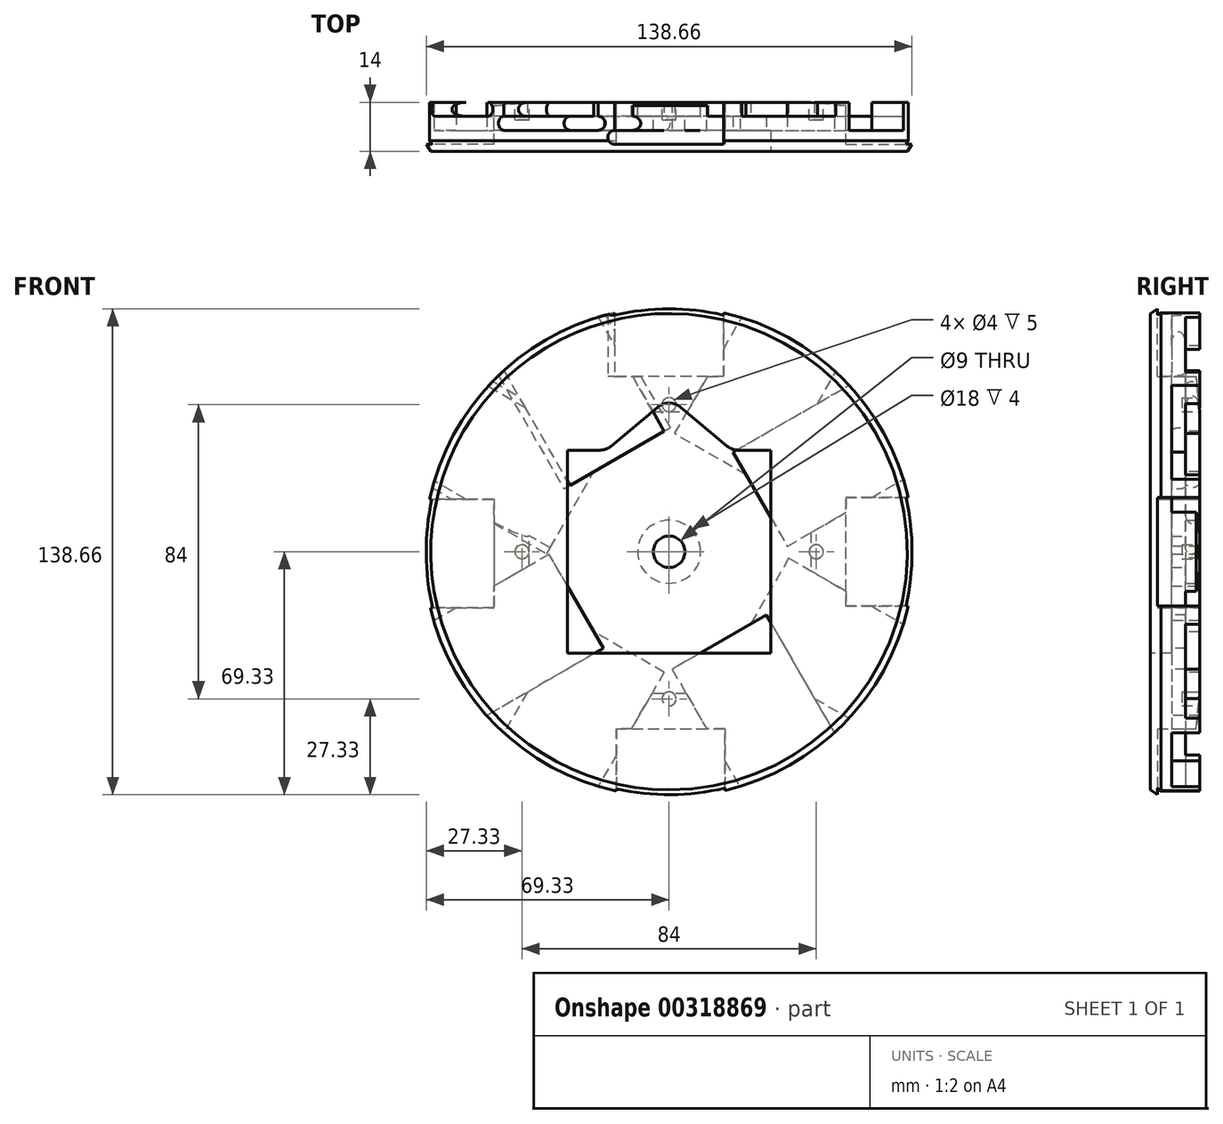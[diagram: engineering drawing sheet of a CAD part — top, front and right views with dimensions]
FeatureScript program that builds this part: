
annotation { "Feature Type Name" : "Feature", "Feature Type Description" : "" }
export const myFeature = defineFeature(function(context is Context, id is Id, definition is map)
    precondition{}
    {
        {
            var Q0;
            Q0=qCreatedBy(makeId("Front.planeOp"),FACE);
            var sketch = newSketch(context, id + "F0", { "sketchPlane" : qUnion([Q0])});
            skCircle(sketch, "E0", {"center": v(0, 0) * mm, "radius": 70 * mm});
            skCircle(sketch, "E1", {"center": v(0, 0) * mm, "radius": 50 * mm});
            skLineSegment(sketch, "E2", {"start": v(0, 50) * mm, "end": v(15.5, 50) * mm});
            skLineSegment(sketch, "E3.MirrorCS", {"start": v(0, 50) * mm, "end": v(-15.5, 50) * mm});
            skLineSegment(sketch, "E4", {"start": v(-15.5, 50) * mm, "end": v(-15.5, 87.34) * mm});
            skLineSegment(sketch, "E5.MirrorCS", {"start": v(15.5, 50) * mm, "end": v(15.5, 87.34) * mm});
            skCircle(sketch, "E6", {"center": v(0, 0) * mm, "radius": 30 * mm, "construction": true});
            skLineSegment(sketch, "E7", {"start": v(0, 0) * mm, "end": v(15, 25.98) * mm, "construction": true});
            skLineSegment(sketch, "E8", {"start": v(15, 25.98) * mm, "end": v(0, 0) * mm, "construction": true});
            skPoint(sketch, "E9.endSnap0", {"position": v(7.5, 13) * mm});
            skLineSegment(sketch, "E10", {"start": v(15, 25.98) * mm, "end": v(1.58, 33.73) * mm});
            skLineSegment(sketch, "E11.MirrorCS", {"start": v(15, 25.98) * mm, "end": v(28.42, 18.23) * mm});
            skLineSegment(sketch, "E12", {"start": v(1.58, 33.73) * mm, "end": v(33.76, 89.47) * mm});
            skLineSegment(sketch, "E13.MirrorCS", {"start": v(28.42, 18.23) * mm, "end": v(60.6, 73.97) * mm});
            skPoint(sketch, "E14.center", {"position": v(0, 10) * mm});
            skLineSegment(sketch, "E15", {"start": v(0, 0) * mm, "end": v(25.98, 15) * mm, "construction": true});
            skLineSegment(sketch, "E16", {"start": v(25.98, 15) * mm, "end": v(18.23, 28.42) * mm});
            skPoint(sketch, "E16.endSnap0", {"position": v(21.71, 22.1) * mm});
            skLineSegment(sketch, "E17", {"start": v(18.23, 28.42) * mm, "end": v(69.8, 58.2) * mm});
            skLineSegment(sketch, "E18.MirrorCS", {"start": v(25.98, 15) * mm, "end": v(33.73, 1.58) * mm});
            skLineSegment(sketch, "E19.MirrorCS", {"start": v(33.73, 1.58) * mm, "end": v(85.3, 31.35) * mm});
            skLineSegment(sketch, "E20.1.0", {"start": v(-50, -16) * mm, "end": v(-87.34, -16) * mm});
            skLineSegment(sketch, "E20.1.1", {"start": v(-50, -0.5) * mm, "end": v(-50, -16) * mm});
            skLineSegment(sketch, "E20.1.2", {"start": v(-50, -0.5) * mm, "end": v(-50, 15) * mm});
            skLineSegment(sketch, "E20.1.3", {"start": v(-50, 15) * mm, "end": v(-87.34, 15) * mm});
            skLineSegment(sketch, "E20.2.0", {"start": v(16, -50.5) * mm, "end": v(16, -87.84) * mm});
            skLineSegment(sketch, "E20.2.1", {"start": v(0.5, -50.5) * mm, "end": v(16, -50.5) * mm});
            skLineSegment(sketch, "E20.2.2", {"start": v(0.5, -50.5) * mm, "end": v(-15, -50.5) * mm});
            skLineSegment(sketch, "E20.2.3", {"start": v(-15, -50.5) * mm, "end": v(-15, -87.84) * mm});
            skLineSegment(sketch, "E20.3.0", {"start": v(50.5, 15.5) * mm, "end": v(87.84, 15.5) * mm});
            skLineSegment(sketch, "E20.3.1", {"start": v(50.5, 0) * mm, "end": v(50.5, 15.5) * mm});
            skLineSegment(sketch, "E20.3.2", {"start": v(50.5, 0) * mm, "end": v(50.5, -15.5) * mm});
            skLineSegment(sketch, "E20.3.3", {"start": v(50.5, -15.5) * mm, "end": v(87.84, -15.5) * mm});
            skPoint(sketch, "E20.center", {"position": v(0.25, -0.25) * mm});
            skLineSegment(sketch, "E21.1.0", {"start": v(-33.98, 1.14) * mm, "end": v(-89.72, 33.33) * mm});
            skLineSegment(sketch, "E21.1.1", {"start": v(-26.23, 14.57) * mm, "end": v(-33.98, 1.14) * mm});
            skLineSegment(sketch, "E21.1.2", {"start": v(-26.23, 14.57) * mm, "end": v(-18.48, 28) * mm});
            skLineSegment(sketch, "E21.1.3", {"start": v(-18.48, 28) * mm, "end": v(-74.22, 60.17) * mm});
            skLineSegment(sketch, "E21.2.0", {"start": v(-1.4, -34.41) * mm, "end": v(-33.58, -90.16) * mm});
            skLineSegment(sketch, "E21.2.1", {"start": v(-14.82, -26.66) * mm, "end": v(-1.4, -34.41) * mm});
            skLineSegment(sketch, "E21.2.2", {"start": v(-14.82, -26.66) * mm, "end": v(-28.24, -18.91) * mm});
            skLineSegment(sketch, "E21.2.3", {"start": v(-28.24, -18.91) * mm, "end": v(-60.42, -74.66) * mm});
            skLineSegment(sketch, "E21.3.0", {"start": v(34.16, -1.83) * mm, "end": v(89.9, -34) * mm});
            skLineSegment(sketch, "E21.3.1", {"start": v(26.41, -15.25) * mm, "end": v(34.16, -1.83) * mm});
            skLineSegment(sketch, "E21.3.2", {"start": v(26.41, -15.25) * mm, "end": v(18.66, -28.67) * mm});
            skLineSegment(sketch, "E21.3.3", {"start": v(18.66, -28.67) * mm, "end": v(74.4, -60.86) * mm});
            skPoint(sketch, "E21.center", {"position": v(0.1, -0.34) * mm});
            skLineSegment(sketch, "E22.1.0", {"start": v(-28.24, 18.91) * mm, "end": v(-58.01, 70.48) * mm});
            skLineSegment(sketch, "E22.1.1", {"start": v(-14.82, 26.66) * mm, "end": v(-28.24, 18.91) * mm});
            skLineSegment(sketch, "E22.1.2", {"start": v(-14.82, 26.66) * mm, "end": v(-1.4, 34.41) * mm});
            skLineSegment(sketch, "E22.1.3", {"start": v(-1.4, 34.41) * mm, "end": v(-31.17, 85.98) * mm});
            skLineSegment(sketch, "E22.2.0", {"start": v(-18.73, -27.56) * mm, "end": v(-70.3, -57.33) * mm});
            skLineSegment(sketch, "E22.2.1", {"start": v(-26.48, -14.13) * mm, "end": v(-18.73, -27.56) * mm});
            skLineSegment(sketch, "E22.2.2", {"start": v(-26.48, -14.13) * mm, "end": v(-34.23, -0.71) * mm});
            skLineSegment(sketch, "E22.2.3", {"start": v(-34.23, -0.71) * mm, "end": v(-85.8, -30.48) * mm});
            skLineSegment(sketch, "E22.3.0", {"start": v(27.74, -18.05) * mm, "end": v(57.51, -69.62) * mm});
            skLineSegment(sketch, "E22.3.1", {"start": v(14.32, -25.8) * mm, "end": v(27.74, -18.05) * mm});
            skLineSegment(sketch, "E22.3.2", {"start": v(14.32, -25.8) * mm, "end": v(0.9, -33.55) * mm});
            skLineSegment(sketch, "E22.3.3", {"start": v(0.9, -33.55) * mm, "end": v(30.67, -85.12) * mm});
            skPoint(sketch, "E22.center", {"position": v(-0.25, 0.43) * mm});
            skCircle(sketch, "E23", {"center": v(0, 0) * mm, "radius": 4.5 * mm});
            skSolve(sketch);
        }
        {
            var Q0;
            {var subQ9=sQuery(id+"F0.wireOp",EDGE,"E10");Q0=makeQuery(id+"F0.imprint","IMPRINT",FACE,{"disambiguationData":[TD([[makeQuery(id+"F0.imprint","IMPRINT",EDGE,{"derivedFrom":subQ9}),1.0]])]});}
            var Q1;
            {var subQ0=sQuery(id+"F0.wireOp",EDGE,"E21.1.1");Q1=makeQuery(id+"F0.imprint","IMPRINT",FACE,{"disambiguationData":[TD([[makeQuery(id+"F0.imprint","IMPRINT",EDGE,{"derivedFrom":subQ0}),-1.0]])]});}
            var Q2;
            {var subQ6=sQuery(id+"F0.wireOp",EDGE,"E0");var subQ12=sQuery(id+"F0.wireOp",EDGE,"E21.1.3");var subQ13=makeQuery(id+"F0.imprint","INTERSECT",VERTEX,{"derivedFrom":[subQ6,subQ12]});Q2=makeQuery(id+"F0.imprint","IMPRINT",FACE,{"disambiguationData":[TD([[makeQuery(id+"F0.imprint","IMPRINT",EDGE,{"disambiguationData":[TD([[subQ13,-1.0]])],"derivedFrom":subQ6}),1.0]])]});}
            var Q3;
            {var subQ0=sQuery(id+"F0.wireOp",EDGE,"E21.1.0");var subQ1=sQuery(id+"F0.wireOp",EDGE,"E0");var subQ2=makeQuery(id+"F0.imprint","INTERSECT",VERTEX,{"derivedFrom":[subQ1,subQ0]});Q3=makeQuery(id+"F0.imprint","IMPRINT",FACE,{"disambiguationData":[TD([[makeQuery(id+"F0.imprint","IMPRINT",EDGE,{"disambiguationData":[TD([[subQ2,-1.0]])],"derivedFrom":subQ1}),1.0]])]});}
            var Q4;
            {var subQ1=sQuery(id+"F0.wireOp",EDGE,"E1");var subQ3=sQuery(id+"F0.wireOp",EDGE,"E21.1.0");var subQ4=makeQuery(id+"F0.imprint","INTERSECT",VERTEX,{"derivedFrom":[subQ1,subQ3]});Q4=makeQuery(id+"F0.imprint","IMPRINT",FACE,{"disambiguationData":[TD([[makeQuery(id+"F0.imprint","IMPRINT",EDGE,{"disambiguationData":[TD([[subQ4,-1.0]])],"derivedFrom":subQ3}),1.0]])]});}
            var Q5;
            {var subQ1=sQuery(id+"F0.wireOp",EDGE,"E1");var subQ3=sQuery(id+"F0.wireOp",EDGE,"E22.2.3");var subQ4=makeQuery(id+"F0.imprint","INTERSECT",VERTEX,{"derivedFrom":[subQ1,subQ3]});Q5=makeQuery(id+"F0.imprint","IMPRINT",FACE,{"disambiguationData":[TD([[makeQuery(id+"F0.imprint","IMPRINT",EDGE,{"disambiguationData":[TD([[subQ4,-1.0]])],"derivedFrom":subQ3}),-1.0]])]});}
            var Q6;
            {var subQ3=sQuery(id+"F0.wireOp",EDGE,"E22.2.3");var subQ6=sQuery(id+"F0.wireOp",EDGE,"E0");var subQ14=makeQuery(id+"F0.imprint","INTERSECT",VERTEX,{"derivedFrom":[subQ6,subQ3]});Q6=makeQuery(id+"F0.imprint","IMPRINT",FACE,{"disambiguationData":[TD([[makeQuery(id+"F0.imprint","IMPRINT",EDGE,{"disambiguationData":[TD([[subQ14,-1.0]])],"derivedFrom":subQ6}),1.0]])]});}
            var Q7;
            {var subQ0=sQuery(id+"F0.wireOp",EDGE,"E22.2.2");Q7=makeQuery(id+"F0.imprint","IMPRINT",FACE,{"disambiguationData":[TD([[makeQuery(id+"F0.imprint","IMPRINT",EDGE,{"derivedFrom":subQ0}),1.0]])]});}
            var Q8;
            {var subQ0=sQuery(id+"F0.wireOp",EDGE,"E20.1.0");var subQ1=sQuery(id+"F0.wireOp",EDGE,"E0");var subQ2=makeQuery(id+"F0.imprint","INTERSECT",VERTEX,{"derivedFrom":[subQ1,subQ0]});Q8=makeQuery(id+"F0.imprint","IMPRINT",FACE,{"disambiguationData":[TD([[makeQuery(id+"F0.imprint","IMPRINT",EDGE,{"disambiguationData":[TD([[subQ2,-1.0]])],"derivedFrom":subQ1}),1.0]])]});}
            var Q9;
            {var subQ0=sQuery(id+"F0.wireOp",EDGE,"E22.2.0");var subQ1=sQuery(id+"F0.wireOp",EDGE,"E0");var subQ2=makeQuery(id+"F0.imprint","INTERSECT",VERTEX,{"derivedFrom":[subQ1,subQ0]});Q9=makeQuery(id+"F0.imprint","IMPRINT",FACE,{"disambiguationData":[TD([[makeQuery(id+"F0.imprint","IMPRINT",EDGE,{"disambiguationData":[TD([[subQ2,-1.0]])],"derivedFrom":subQ1}),1.0]])]});}
            var Q10;
            {var subQ0=sQuery(id+"F0.wireOp",EDGE,"E21.2.0");var subQ1=sQuery(id+"F0.wireOp",EDGE,"E0");var subQ2=makeQuery(id+"F0.imprint","INTERSECT",VERTEX,{"derivedFrom":[subQ1,subQ0]});Q10=makeQuery(id+"F0.imprint","IMPRINT",FACE,{"disambiguationData":[TD([[makeQuery(id+"F0.imprint","IMPRINT",EDGE,{"disambiguationData":[TD([[subQ2,-1.0]])],"derivedFrom":subQ1}),1.0]])]});}
            var Q11;
            {var subQ0=sQuery(id+"F0.wireOp",EDGE,"E21.2.3");var subQ3=sQuery(id+"F0.wireOp",EDGE,"E1");var subQ4=makeQuery(id+"F0.imprint","INTERSECT",VERTEX,{"derivedFrom":[subQ3,subQ0]});Q11=makeQuery(id+"F0.imprint","IMPRINT",FACE,{"disambiguationData":[TD([[makeQuery(id+"F0.imprint","IMPRINT",EDGE,{"disambiguationData":[TD([[subQ4,-1.0]])],"derivedFrom":subQ3}),1.0]])]});}
            var Q12;
            {var subQ0=sQuery(id+"F0.wireOp",EDGE,"E21.2.1");Q12=makeQuery(id+"F0.imprint","IMPRINT",FACE,{"disambiguationData":[TD([[makeQuery(id+"F0.imprint","IMPRINT",EDGE,{"derivedFrom":subQ0}),-1.0]])]});}
            var Q13;
            {var subQ0=sQuery(id+"F0.wireOp",EDGE,"E21.2.3");var subQ1=sQuery(id+"F0.wireOp",EDGE,"E1");var subQ2=makeQuery(id+"F0.imprint","INTERSECT",VERTEX,{"derivedFrom":[subQ1,subQ0]});Q13=makeQuery(id+"F0.imprint","IMPRINT",FACE,{"disambiguationData":[TD([[makeQuery(id+"F0.imprint","IMPRINT",EDGE,{"disambiguationData":[TD([[subQ2,-1.0]])],"derivedFrom":subQ1}),-1.0]])]});}
            var Q14;
            {var subQ9=sQuery(id+"F0.wireOp",EDGE,"E21.2.3");var subQ10=sQuery(id+"F0.wireOp",EDGE,"E0");var subQ11=makeQuery(id+"F0.imprint","INTERSECT",VERTEX,{"derivedFrom":[subQ10,subQ9]});Q14=makeQuery(id+"F0.imprint","IMPRINT",FACE,{"disambiguationData":[TD([[makeQuery(id+"F0.imprint","IMPRINT",EDGE,{"disambiguationData":[TD([[subQ11,-1.0]])],"derivedFrom":subQ10}),1.0]])]});}
            var Q15;
            {var subQ1=sQuery(id+"F0.wireOp",EDGE,"E1");var subQ3=sQuery(id+"F0.wireOp",EDGE,"E21.2.0");var subQ4=makeQuery(id+"F0.imprint","INTERSECT",VERTEX,{"derivedFrom":[subQ1,subQ3]});Q15=makeQuery(id+"F0.imprint","IMPRINT",FACE,{"disambiguationData":[TD([[makeQuery(id+"F0.imprint","IMPRINT",EDGE,{"disambiguationData":[TD([[subQ4,-1.0]])],"derivedFrom":subQ3}),1.0]])]});}
            var Q16;
            {var subQ1=sQuery(id+"F0.wireOp",EDGE,"E1");var subQ3=sQuery(id+"F0.wireOp",EDGE,"E22.3.3");var subQ4=makeQuery(id+"F0.imprint","INTERSECT",VERTEX,{"derivedFrom":[subQ1,subQ3]});Q16=makeQuery(id+"F0.imprint","IMPRINT",FACE,{"disambiguationData":[TD([[makeQuery(id+"F0.imprint","IMPRINT",EDGE,{"disambiguationData":[TD([[subQ4,-1.0]])],"derivedFrom":subQ3}),-1.0]])]});}
            var Q17;
            {var subQ0=sQuery(id+"F0.wireOp",EDGE,"E20.2.0");var subQ1=sQuery(id+"F0.wireOp",EDGE,"E0");var subQ2=makeQuery(id+"F0.imprint","INTERSECT",VERTEX,{"derivedFrom":[subQ1,subQ0]});Q17=makeQuery(id+"F0.imprint","IMPRINT",FACE,{"disambiguationData":[TD([[makeQuery(id+"F0.imprint","IMPRINT",EDGE,{"disambiguationData":[TD([[subQ2,-1.0]])],"derivedFrom":subQ1}),1.0]])]});}
            var Q18;
            {var subQ0=sQuery(id+"F0.wireOp",EDGE,"E22.3.2");Q18=makeQuery(id+"F0.imprint","IMPRINT",FACE,{"disambiguationData":[TD([[makeQuery(id+"F0.imprint","IMPRINT",EDGE,{"derivedFrom":subQ0}),1.0]])]});}
            var Q19;
            {var subQ3=sQuery(id+"F0.wireOp",EDGE,"E22.3.3");var subQ12=sQuery(id+"F0.wireOp",EDGE,"E0");var subQ13=makeQuery(id+"F0.imprint","INTERSECT",VERTEX,{"derivedFrom":[subQ12,subQ3]});Q19=makeQuery(id+"F0.imprint","IMPRINT",FACE,{"disambiguationData":[TD([[makeQuery(id+"F0.imprint","IMPRINT",EDGE,{"disambiguationData":[TD([[subQ13,-1.0]])],"derivedFrom":subQ12}),1.0]])]});}
            var Q20;
            {var subQ0=sQuery(id+"F0.wireOp",EDGE,"E21.3.3");var subQ3=sQuery(id+"F0.wireOp",EDGE,"E1");var subQ4=makeQuery(id+"F0.imprint","INTERSECT",VERTEX,{"derivedFrom":[subQ3,subQ0]});Q20=makeQuery(id+"F0.imprint","IMPRINT",FACE,{"disambiguationData":[TD([[makeQuery(id+"F0.imprint","IMPRINT",EDGE,{"disambiguationData":[TD([[subQ4,-1.0]])],"derivedFrom":subQ3}),1.0]])]});}
            var Q21;
            {var subQ0=sQuery(id+"F0.wireOp",EDGE,"E21.3.1");Q21=makeQuery(id+"F0.imprint","IMPRINT",FACE,{"disambiguationData":[TD([[makeQuery(id+"F0.imprint","IMPRINT",EDGE,{"derivedFrom":subQ0}),-1.0]])]});}
            var Q22;
            {var subQ0=sQuery(id+"F0.wireOp",EDGE,"E21.3.3");var subQ1=sQuery(id+"F0.wireOp",EDGE,"E1");var subQ2=makeQuery(id+"F0.imprint","INTERSECT",VERTEX,{"derivedFrom":[subQ1,subQ0]});Q22=makeQuery(id+"F0.imprint","IMPRINT",FACE,{"disambiguationData":[TD([[makeQuery(id+"F0.imprint","IMPRINT",EDGE,{"disambiguationData":[TD([[subQ2,-1.0]])],"derivedFrom":subQ1}),-1.0]])]});}
            var Q23;
            {var subQ0=sQuery(id+"F0.wireOp",EDGE,"E22.3.0");var subQ1=sQuery(id+"F0.wireOp",EDGE,"E0");var subQ2=makeQuery(id+"F0.imprint","INTERSECT",VERTEX,{"derivedFrom":[subQ1,subQ0]});Q23=makeQuery(id+"F0.imprint","IMPRINT",FACE,{"disambiguationData":[TD([[makeQuery(id+"F0.imprint","IMPRINT",EDGE,{"disambiguationData":[TD([[subQ2,-1.0]])],"derivedFrom":subQ1}),1.0]])]});}
            var Q24;
            {var subQ10=sQuery(id+"F0.wireOp",EDGE,"E0");var subQ12=sQuery(id+"F0.wireOp",EDGE,"E21.3.3");var subQ13=makeQuery(id+"F0.imprint","INTERSECT",VERTEX,{"derivedFrom":[subQ10,subQ12]});Q24=makeQuery(id+"F0.imprint","IMPRINT",FACE,{"disambiguationData":[TD([[makeQuery(id+"F0.imprint","IMPRINT",EDGE,{"disambiguationData":[TD([[subQ13,-1.0]])],"derivedFrom":subQ10}),1.0]])]});}
            var Q25;
            {var subQ1=sQuery(id+"F0.wireOp",EDGE,"E1");var subQ3=sQuery(id+"F0.wireOp",EDGE,"E21.3.0");var subQ4=makeQuery(id+"F0.imprint","INTERSECT",VERTEX,{"derivedFrom":[subQ1,subQ3]});Q25=makeQuery(id+"F0.imprint","IMPRINT",FACE,{"disambiguationData":[TD([[makeQuery(id+"F0.imprint","IMPRINT",EDGE,{"disambiguationData":[TD([[subQ4,-1.0]])],"derivedFrom":subQ3}),1.0]])]});}
            var Q26;
            {var subQ1=sQuery(id+"F0.wireOp",EDGE,"E1");var subQ3=sQuery(id+"F0.wireOp",EDGE,"E19.MirrorCS");var subQ4=makeQuery(id+"F0.imprint","INTERSECT",VERTEX,{"derivedFrom":[subQ1,subQ3]});Q26=makeQuery(id+"F0.imprint","IMPRINT",FACE,{"disambiguationData":[TD([[makeQuery(id+"F0.imprint","IMPRINT",EDGE,{"disambiguationData":[TD([[subQ4,-1.0]])],"derivedFrom":subQ3}),-1.0]])]});}
            var Q27;
            {var subQ0=sQuery(id+"F0.wireOp",EDGE,"E18.MirrorCS");Q27=makeQuery(id+"F0.imprint","IMPRINT",FACE,{"disambiguationData":[TD([[makeQuery(id+"F0.imprint","IMPRINT",EDGE,{"derivedFrom":subQ0}),1.0]])]});}
            var Q28;
            {var subQ5=sQuery(id+"F0.wireOp",EDGE,"E19.MirrorCS");var subQ6=sQuery(id+"F0.wireOp",EDGE,"E0");var subQ7=makeQuery(id+"F0.imprint","INTERSECT",VERTEX,{"derivedFrom":[subQ6,subQ5]});Q28=makeQuery(id+"F0.imprint","IMPRINT",FACE,{"disambiguationData":[TD([[makeQuery(id+"F0.imprint","IMPRINT",EDGE,{"disambiguationData":[TD([[subQ7,-1.0]])],"derivedFrom":subQ6}),1.0]])]});}
            var Q29;
            {var subQ0=sQuery(id+"F0.wireOp",EDGE,"E19.MirrorCS");var subQ1=sQuery(id+"F0.wireOp",EDGE,"E0");var subQ2=makeQuery(id+"F0.imprint","INTERSECT",VERTEX,{"derivedFrom":[subQ1,subQ0]});Q29=makeQuery(id+"F0.imprint","IMPRINT",FACE,{"disambiguationData":[TD([[makeQuery(id+"F0.imprint","IMPRINT",EDGE,{"disambiguationData":[TD([[subQ2,1.0]])],"derivedFrom":subQ1}),1.0]])]});}
            var Q30;
            {var subQ5=sQuery(id+"F0.wireOp",EDGE,"E13.MirrorCS");var subQ7=sQuery(id+"F0.wireOp",EDGE,"E1");var subQ8=makeQuery(id+"F0.imprint","INTERSECT",VERTEX,{"derivedFrom":[subQ7,subQ5]});Q30=makeQuery(id+"F0.imprint","IMPRINT",FACE,{"disambiguationData":[TD([[makeQuery(id+"F0.imprint","IMPRINT",EDGE,{"disambiguationData":[TD([[subQ8,-1.0]])],"derivedFrom":subQ7}),1.0]])]});}
            var Q31;
            {var subQ1=sQuery(id+"F0.wireOp",EDGE,"E10");Q31=makeQuery(id+"F0.imprint","IMPRINT",FACE,{"disambiguationData":[TD([[makeQuery(id+"F0.imprint","IMPRINT",EDGE,{"derivedFrom":subQ1}),-1.0]])]});}
            var Q32;
            {var subQ0=sQuery(id+"F0.wireOp",EDGE,"E13.MirrorCS");var subQ1=sQuery(id+"F0.wireOp",EDGE,"E1");var subQ2=makeQuery(id+"F0.imprint","INTERSECT",VERTEX,{"derivedFrom":[subQ1,subQ0]});Q32=makeQuery(id+"F0.imprint","IMPRINT",FACE,{"disambiguationData":[TD([[makeQuery(id+"F0.imprint","IMPRINT",EDGE,{"disambiguationData":[TD([[subQ2,-1.0]])],"derivedFrom":subQ1}),-1.0]])]});}
            var Q33;
            {var subQ5=sQuery(id+"F0.wireOp",EDGE,"E13.MirrorCS");var subQ6=sQuery(id+"F0.wireOp",EDGE,"E0");var subQ7=makeQuery(id+"F0.imprint","INTERSECT",VERTEX,{"derivedFrom":[subQ6,subQ5]});Q33=makeQuery(id+"F0.imprint","IMPRINT",FACE,{"disambiguationData":[TD([[makeQuery(id+"F0.imprint","IMPRINT",EDGE,{"disambiguationData":[TD([[subQ7,-1.0]])],"derivedFrom":subQ6}),1.0]])]});}
            var Q34;
            {var subQ0=sQuery(id+"F0.wireOp",EDGE,"E17");var subQ1=sQuery(id+"F0.wireOp",EDGE,"E0");var subQ2=makeQuery(id+"F0.imprint","INTERSECT",VERTEX,{"derivedFrom":[subQ1,subQ0]});Q34=makeQuery(id+"F0.imprint","IMPRINT",FACE,{"disambiguationData":[TD([[makeQuery(id+"F0.imprint","IMPRINT",EDGE,{"disambiguationData":[TD([[subQ2,-1.0]])],"derivedFrom":subQ1}),1.0]])]});}
            var Q35;
            {var subQ0=sQuery(id+"F0.wireOp",EDGE,"E12");var subQ1=sQuery(id+"F0.wireOp",EDGE,"E0");var subQ2=makeQuery(id+"F0.imprint","INTERSECT",VERTEX,{"derivedFrom":[subQ1,subQ0]});Q35=makeQuery(id+"F0.imprint","IMPRINT",FACE,{"disambiguationData":[TD([[makeQuery(id+"F0.imprint","IMPRINT",EDGE,{"disambiguationData":[TD([[subQ2,-1.0]])],"derivedFrom":subQ1}),1.0]])]});}
            var Q36;
            {var subQ1=sQuery(id+"F0.wireOp",EDGE,"E1");var subQ3=sQuery(id+"F0.wireOp",EDGE,"E12");var subQ4=makeQuery(id+"F0.imprint","INTERSECT",VERTEX,{"derivedFrom":[subQ1,subQ3]});Q36=makeQuery(id+"F0.imprint","IMPRINT",FACE,{"disambiguationData":[TD([[makeQuery(id+"F0.imprint","IMPRINT",EDGE,{"disambiguationData":[TD([[subQ4,-1.0]])],"derivedFrom":subQ3}),1.0]])]});}
            var Q37;
            {var subQ1=sQuery(id+"F0.wireOp",EDGE,"E1");var subQ3=sQuery(id+"F0.wireOp",EDGE,"E22.1.3");var subQ4=makeQuery(id+"F0.imprint","INTERSECT",VERTEX,{"derivedFrom":[subQ1,subQ3]});Q37=makeQuery(id+"F0.imprint","IMPRINT",FACE,{"disambiguationData":[TD([[makeQuery(id+"F0.imprint","IMPRINT",EDGE,{"disambiguationData":[TD([[subQ4,-1.0]])],"derivedFrom":subQ3}),-1.0]])]});}
            var Q38;
            {var subQ0=sQuery(id+"F0.wireOp",EDGE,"E22.1.2");Q38=makeQuery(id+"F0.imprint","IMPRINT",FACE,{"disambiguationData":[TD([[makeQuery(id+"F0.imprint","IMPRINT",EDGE,{"derivedFrom":subQ0}),1.0]])]});}
            var Q39;
            {var subQ0=sQuery(id+"F0.wireOp",EDGE,"E21.1.3");var subQ3=sQuery(id+"F0.wireOp",EDGE,"E1");var subQ4=makeQuery(id+"F0.imprint","INTERSECT",VERTEX,{"derivedFrom":[subQ3,subQ0]});Q39=makeQuery(id+"F0.imprint","IMPRINT",FACE,{"disambiguationData":[TD([[makeQuery(id+"F0.imprint","IMPRINT",EDGE,{"disambiguationData":[TD([[subQ4,-1.0]])],"derivedFrom":subQ3}),1.0]])]});}
            var Q40;
            {var subQ0=sQuery(id+"F0.wireOp",EDGE,"E21.1.3");var subQ1=sQuery(id+"F0.wireOp",EDGE,"E1");var subQ2=makeQuery(id+"F0.imprint","INTERSECT",VERTEX,{"derivedFrom":[subQ1,subQ0]});Q40=makeQuery(id+"F0.imprint","IMPRINT",FACE,{"disambiguationData":[TD([[makeQuery(id+"F0.imprint","IMPRINT",EDGE,{"disambiguationData":[TD([[subQ2,-1.0]])],"derivedFrom":subQ1}),-1.0]])]});}
            var Q41;
            {var subQ0=sQuery(id+"F0.wireOp",EDGE,"E22.1.0");var subQ1=sQuery(id+"F0.wireOp",EDGE,"E0");var subQ2=makeQuery(id+"F0.imprint","INTERSECT",VERTEX,{"derivedFrom":[subQ1,subQ0]});Q41=makeQuery(id+"F0.imprint","IMPRINT",FACE,{"disambiguationData":[TD([[makeQuery(id+"F0.imprint","IMPRINT",EDGE,{"disambiguationData":[TD([[subQ2,-1.0]])],"derivedFrom":subQ1}),1.0]])]});}
            var Q42;
            {var subQ3=sQuery(id+"F0.wireOp",EDGE,"E22.1.3");var subQ10=sQuery(id+"F0.wireOp",EDGE,"E0");var subQ11=makeQuery(id+"F0.imprint","INTERSECT",VERTEX,{"derivedFrom":[subQ10,subQ3]});Q42=makeQuery(id+"F0.imprint","IMPRINT",FACE,{"disambiguationData":[TD([[makeQuery(id+"F0.imprint","IMPRINT",EDGE,{"disambiguationData":[TD([[subQ11,-1.0]])],"derivedFrom":subQ10}),1.0]])]});}
            var Q43;
            {var subQ0=sQuery(id+"F0.wireOp",EDGE,"E4");var subQ1=sQuery(id+"F0.wireOp",EDGE,"E0");var subQ2=makeQuery(id+"F0.imprint","INTERSECT",VERTEX,{"derivedFrom":[subQ1,subQ0]});Q43=makeQuery(id+"F0.imprint","IMPRINT",FACE,{"disambiguationData":[TD([[makeQuery(id+"F0.imprint","IMPRINT",EDGE,{"disambiguationData":[TD([[subQ2,-1.0]])],"derivedFrom":subQ1}),1.0]])]});}
            var Q44;
            {var subQ0=sQuery(id+"F0.wireOp",EDGE,"E21.3.0");var subQ1=sQuery(id+"F0.wireOp",EDGE,"E0");var subQ2=makeQuery(id+"F0.imprint","INTERSECT",VERTEX,{"derivedFrom":[subQ1,subQ0]});Q44=makeQuery(id+"F0.imprint","IMPRINT",FACE,{"disambiguationData":[TD([[makeQuery(id+"F0.imprint","IMPRINT",EDGE,{"disambiguationData":[TD([[subQ2,-1.0]])],"derivedFrom":subQ1}),1.0]])]});}
            var Q45;
            {var subQ0=sQuery(id+"F0.wireOp",EDGE,"E4");var subQ1=sQuery(id+"F0.wireOp",EDGE,"E3.MirrorCS");var subQ2=makeQuery(id+"F0.imprint","INTERSECT",VERTEX,{"derivedFrom":[subQ1,subQ0]});Q45=makeQuery(id+"F0.imprint","IMPRINT",FACE,{"disambiguationData":[TD([[makeQuery(id+"F0.imprint","IMPRINT",EDGE,{"disambiguationData":[TD([[subQ2,1.0]])],"derivedFrom":subQ1}),-1.0]])]});}
            var Q46;
            {var subQ7=sQuery(id+"F0.wireOp",EDGE,"E5.MirrorCS");var subQ11=sQuery(id+"F0.wireOp",EDGE,"E0");var subQ13=makeQuery(id+"F0.imprint","INTERSECT",VERTEX,{"derivedFrom":[subQ11,subQ7]});Q46=makeQuery(id+"F0.imprint","IMPRINT",FACE,{"disambiguationData":[TD([[makeQuery(id+"F0.imprint","IMPRINT",EDGE,{"disambiguationData":[TD([[subQ13,-1.0]])],"derivedFrom":subQ11}),1.0]])]});}
            var Q47;
            {var subQ0=sQuery(id+"F0.wireOp",EDGE,"E5.MirrorCS");var subQ1=sQuery(id+"F0.wireOp",EDGE,"E2");var subQ2=makeQuery(id+"F0.imprint","INTERSECT",VERTEX,{"derivedFrom":[subQ1,subQ0]});Q47=makeQuery(id+"F0.imprint","IMPRINT",FACE,{"disambiguationData":[TD([[makeQuery(id+"F0.imprint","IMPRINT",EDGE,{"disambiguationData":[TD([[subQ2,1.0]])],"derivedFrom":subQ1}),1.0]])]});}
            var Q48;
            {var subQ6=sQuery(id+"F0.wireOp",EDGE,"E0");var subQ11=sQuery(id+"F0.wireOp",EDGE,"E20.1.3");var subQ13=makeQuery(id+"F0.imprint","INTERSECT",VERTEX,{"derivedFrom":[subQ6,subQ11]});Q48=makeQuery(id+"F0.imprint","IMPRINT",FACE,{"disambiguationData":[TD([[makeQuery(id+"F0.imprint","IMPRINT",EDGE,{"disambiguationData":[TD([[subQ13,-1.0]])],"derivedFrom":subQ6}),1.0]])]});}
            var Q49;
            {var subQ0=sQuery(id+"F0.wireOp",EDGE,"E20.1.3");var subQ1=sQuery(id+"F0.wireOp",EDGE,"E20.1.2");var subQ2=makeQuery(id+"F0.imprint","INTERSECT",VERTEX,{"derivedFrom":[subQ1,subQ0]});Q49=makeQuery(id+"F0.imprint","IMPRINT",FACE,{"disambiguationData":[TD([[makeQuery(id+"F0.imprint","IMPRINT",EDGE,{"disambiguationData":[TD([[subQ2,1.0]])],"derivedFrom":subQ1}),1.0]])]});}
            var Q50;
            {var subQ0=sQuery(id+"F0.wireOp",EDGE,"E20.1.1");var subQ1=sQuery(id+"F0.wireOp",EDGE,"E20.1.0");var subQ2=makeQuery(id+"F0.imprint","INTERSECT",VERTEX,{"derivedFrom":[subQ1,subQ0]});Q50=makeQuery(id+"F0.imprint","IMPRINT",FACE,{"disambiguationData":[TD([[makeQuery(id+"F0.imprint","IMPRINT",EDGE,{"disambiguationData":[TD([[subQ2,-1.0]])],"derivedFrom":subQ1}),-1.0]])]});}
            var Q51;
            {var subQ6=sQuery(id+"F0.wireOp",EDGE,"E0");var subQ11=sQuery(id+"F0.wireOp",EDGE,"E20.2.3");var subQ12=makeQuery(id+"F0.imprint","INTERSECT",VERTEX,{"derivedFrom":[subQ6,subQ11]});Q51=makeQuery(id+"F0.imprint","IMPRINT",FACE,{"disambiguationData":[TD([[makeQuery(id+"F0.imprint","IMPRINT",EDGE,{"disambiguationData":[TD([[subQ12,-1.0]])],"derivedFrom":subQ6}),1.0]])]});}
            var Q52;
            {var subQ0=sQuery(id+"F0.wireOp",EDGE,"E20.2.3");var subQ1=sQuery(id+"F0.wireOp",EDGE,"E20.2.2");var subQ2=makeQuery(id+"F0.imprint","INTERSECT",VERTEX,{"derivedFrom":[subQ1,subQ0]});Q52=makeQuery(id+"F0.imprint","IMPRINT",FACE,{"disambiguationData":[TD([[makeQuery(id+"F0.imprint","IMPRINT",EDGE,{"disambiguationData":[TD([[subQ2,1.0]])],"derivedFrom":subQ1}),1.0]])]});}
            var Q53;
            {var subQ0=sQuery(id+"F0.wireOp",EDGE,"E20.2.1");var subQ1=sQuery(id+"F0.wireOp",EDGE,"E20.2.0");var subQ2=makeQuery(id+"F0.imprint","INTERSECT",VERTEX,{"derivedFrom":[subQ1,subQ0]});Q53=makeQuery(id+"F0.imprint","IMPRINT",FACE,{"disambiguationData":[TD([[makeQuery(id+"F0.imprint","IMPRINT",EDGE,{"disambiguationData":[TD([[subQ2,-1.0]])],"derivedFrom":subQ1}),-1.0]])]});}
            var Q54;
            {var subQ0=sQuery(id+"F0.wireOp",EDGE,"E20.3.3");var subQ1=sQuery(id+"F0.wireOp",EDGE,"E20.3.2");var subQ2=makeQuery(id+"F0.imprint","INTERSECT",VERTEX,{"derivedFrom":[subQ1,subQ0]});Q54=makeQuery(id+"F0.imprint","IMPRINT",FACE,{"disambiguationData":[TD([[makeQuery(id+"F0.imprint","IMPRINT",EDGE,{"disambiguationData":[TD([[subQ2,1.0]])],"derivedFrom":subQ1}),1.0]])]});}
            var Q55;
            {var subQ0=sQuery(id+"F0.wireOp",EDGE,"E20.3.0");var subQ1=sQuery(id+"F0.wireOp",EDGE,"E0");var subQ2=makeQuery(id+"F0.imprint","INTERSECT",VERTEX,{"derivedFrom":[subQ1,subQ0]});Q55=makeQuery(id+"F0.imprint","IMPRINT",FACE,{"disambiguationData":[TD([[makeQuery(id+"F0.imprint","IMPRINT",EDGE,{"disambiguationData":[TD([[subQ2,1.0]])],"derivedFrom":subQ1}),1.0]])]});}
            var Q56;
            {var subQ0=sQuery(id+"F0.wireOp",EDGE,"E20.3.1");var subQ1=sQuery(id+"F0.wireOp",EDGE,"E19.MirrorCS");var subQ2=makeQuery(id+"F0.imprint","INTERSECT",VERTEX,{"derivedFrom":[subQ1,subQ0]});Q56=makeQuery(id+"F0.imprint","IMPRINT",FACE,{"disambiguationData":[TD([[makeQuery(id+"F0.imprint","IMPRINT",EDGE,{"disambiguationData":[TD([[subQ2,-1.0]])],"derivedFrom":subQ1}),1.0]])]});}
            extrude(context, id + "F1", {"entities" : qUnion([Q0, Q1, Q2, Q3, Q4, Q5, Q6, Q7, Q8, Q9, Q10, Q11, Q12, Q13, Q14, Q15, Q16, Q17, Q18, Q19, Q20, Q21, Q22, Q23, Q24, Q25, Q26, Q27, Q28, Q29, Q30, Q31, Q32, Q33, Q34, Q35, Q36, Q37, Q38, Q39, Q40, Q41, Q42, Q43, Q44, Q45, Q46, Q47, Q48, Q49, Q50, Q51, Q52, Q53, Q54, Q55, Q56]), "offsetDistance" : 25 * mm, "depth" : 6 * mm});
        }
        {
            var Q0;
            {var subQ0=sQuery(id+"F0.wireOp",EDGE,"E19.MirrorCS");var subQ1=sQuery(id+"F0.wireOp",EDGE,"E0");var subQ2=makeQuery(id+"F0.imprint","INTERSECT",VERTEX,{"derivedFrom":[subQ1,subQ0]});Q0=makeQuery(id+"F0.imprint","IMPRINT",FACE,{"disambiguationData":[TD([[makeQuery(id+"F0.imprint","IMPRINT",EDGE,{"disambiguationData":[TD([[subQ2,1.0]])],"derivedFrom":subQ1}),1.0]])]});}
            var Q1;
            {var subQ0=sQuery(id+"F0.wireOp",EDGE,"E20.3.0");var subQ1=sQuery(id+"F0.wireOp",EDGE,"E0");var subQ2=makeQuery(id+"F0.imprint","INTERSECT",VERTEX,{"derivedFrom":[subQ1,subQ0]});Q1=makeQuery(id+"F0.imprint","IMPRINT",FACE,{"disambiguationData":[TD([[makeQuery(id+"F0.imprint","IMPRINT",EDGE,{"disambiguationData":[TD([[subQ2,1.0]])],"derivedFrom":subQ1}),1.0]])]});}
            var Q2;
            {var subQ9=sQuery(id+"F0.wireOp",EDGE,"E10");Q2=makeQuery(id+"F0.imprint","IMPRINT",FACE,{"disambiguationData":[TD([[makeQuery(id+"F0.imprint","IMPRINT",EDGE,{"derivedFrom":subQ9}),1.0]])]});}
            var Q3;
            {var subQ1=sQuery(id+"F0.wireOp",EDGE,"E1");var subQ3=sQuery(id+"F0.wireOp",EDGE,"E19.MirrorCS");var subQ4=makeQuery(id+"F0.imprint","INTERSECT",VERTEX,{"derivedFrom":[subQ1,subQ3]});Q3=makeQuery(id+"F0.imprint","IMPRINT",FACE,{"disambiguationData":[TD([[makeQuery(id+"F0.imprint","IMPRINT",EDGE,{"disambiguationData":[TD([[subQ4,-1.0]])],"derivedFrom":subQ3}),-1.0]])]});}
            var Q4;
            {var subQ1=sQuery(id+"F0.wireOp",EDGE,"E1");var subQ3=sQuery(id+"F0.wireOp",EDGE,"E21.3.0");var subQ4=makeQuery(id+"F0.imprint","INTERSECT",VERTEX,{"derivedFrom":[subQ1,subQ3]});Q4=makeQuery(id+"F0.imprint","IMPRINT",FACE,{"disambiguationData":[TD([[makeQuery(id+"F0.imprint","IMPRINT",EDGE,{"disambiguationData":[TD([[subQ4,-1.0]])],"derivedFrom":subQ3}),1.0]])]});}
            var Q5;
            {var subQ1=sQuery(id+"F0.wireOp",EDGE,"E1");var subQ3=sQuery(id+"F0.wireOp",EDGE,"E12");var subQ4=makeQuery(id+"F0.imprint","INTERSECT",VERTEX,{"derivedFrom":[subQ1,subQ3]});Q5=makeQuery(id+"F0.imprint","IMPRINT",FACE,{"disambiguationData":[TD([[makeQuery(id+"F0.imprint","IMPRINT",EDGE,{"disambiguationData":[TD([[subQ4,-1.0]])],"derivedFrom":subQ3}),1.0]])]});}
            var Q6;
            {var subQ1=sQuery(id+"F0.wireOp",EDGE,"E1");var subQ3=sQuery(id+"F0.wireOp",EDGE,"E22.1.3");var subQ4=makeQuery(id+"F0.imprint","INTERSECT",VERTEX,{"derivedFrom":[subQ1,subQ3]});Q6=makeQuery(id+"F0.imprint","IMPRINT",FACE,{"disambiguationData":[TD([[makeQuery(id+"F0.imprint","IMPRINT",EDGE,{"disambiguationData":[TD([[subQ4,-1.0]])],"derivedFrom":subQ3}),-1.0]])]});}
            var Q7;
            {var subQ7=sQuery(id+"F0.wireOp",EDGE,"E5.MirrorCS");var subQ11=sQuery(id+"F0.wireOp",EDGE,"E0");var subQ13=makeQuery(id+"F0.imprint","INTERSECT",VERTEX,{"derivedFrom":[subQ11,subQ7]});Q7=makeQuery(id+"F0.imprint","IMPRINT",FACE,{"disambiguationData":[TD([[makeQuery(id+"F0.imprint","IMPRINT",EDGE,{"disambiguationData":[TD([[subQ13,-1.0]])],"derivedFrom":subQ11}),1.0]])]});}
            var Q8;
            {var subQ0=sQuery(id+"F0.wireOp",EDGE,"E12");var subQ1=sQuery(id+"F0.wireOp",EDGE,"E0");var subQ2=makeQuery(id+"F0.imprint","INTERSECT",VERTEX,{"derivedFrom":[subQ1,subQ0]});Q8=makeQuery(id+"F0.imprint","IMPRINT",FACE,{"disambiguationData":[TD([[makeQuery(id+"F0.imprint","IMPRINT",EDGE,{"disambiguationData":[TD([[subQ2,-1.0]])],"derivedFrom":subQ1}),1.0]])]});}
            var Q9;
            {var subQ0=sQuery(id+"F0.wireOp",EDGE,"E17");var subQ1=sQuery(id+"F0.wireOp",EDGE,"E0");var subQ2=makeQuery(id+"F0.imprint","INTERSECT",VERTEX,{"derivedFrom":[subQ1,subQ0]});Q9=makeQuery(id+"F0.imprint","IMPRINT",FACE,{"disambiguationData":[TD([[makeQuery(id+"F0.imprint","IMPRINT",EDGE,{"disambiguationData":[TD([[subQ2,-1.0]])],"derivedFrom":subQ1}),1.0]])]});}
            var Q10;
            {var subQ0=sQuery(id+"F0.wireOp",EDGE,"E4");var subQ1=sQuery(id+"F0.wireOp",EDGE,"E0");var subQ2=makeQuery(id+"F0.imprint","INTERSECT",VERTEX,{"derivedFrom":[subQ1,subQ0]});Q10=makeQuery(id+"F0.imprint","IMPRINT",FACE,{"disambiguationData":[TD([[makeQuery(id+"F0.imprint","IMPRINT",EDGE,{"disambiguationData":[TD([[subQ2,-1.0]])],"derivedFrom":subQ1}),1.0]])]});}
            var Q11;
            {var subQ0=sQuery(id+"F0.wireOp",EDGE,"E22.1.0");var subQ1=sQuery(id+"F0.wireOp",EDGE,"E0");var subQ2=makeQuery(id+"F0.imprint","INTERSECT",VERTEX,{"derivedFrom":[subQ1,subQ0]});Q11=makeQuery(id+"F0.imprint","IMPRINT",FACE,{"disambiguationData":[TD([[makeQuery(id+"F0.imprint","IMPRINT",EDGE,{"disambiguationData":[TD([[subQ2,-1.0]])],"derivedFrom":subQ1}),1.0]])]});}
            var Q12;
            {var subQ0=sQuery(id+"F0.wireOp",EDGE,"E21.1.0");var subQ1=sQuery(id+"F0.wireOp",EDGE,"E0");var subQ2=makeQuery(id+"F0.imprint","INTERSECT",VERTEX,{"derivedFrom":[subQ1,subQ0]});Q12=makeQuery(id+"F0.imprint","IMPRINT",FACE,{"disambiguationData":[TD([[makeQuery(id+"F0.imprint","IMPRINT",EDGE,{"disambiguationData":[TD([[subQ2,-1.0]])],"derivedFrom":subQ1}),1.0]])]});}
            var Q13;
            {var subQ1=sQuery(id+"F0.wireOp",EDGE,"E1");var subQ3=sQuery(id+"F0.wireOp",EDGE,"E21.1.0");var subQ4=makeQuery(id+"F0.imprint","INTERSECT",VERTEX,{"derivedFrom":[subQ1,subQ3]});Q13=makeQuery(id+"F0.imprint","IMPRINT",FACE,{"disambiguationData":[TD([[makeQuery(id+"F0.imprint","IMPRINT",EDGE,{"disambiguationData":[TD([[subQ4,-1.0]])],"derivedFrom":subQ3}),1.0]])]});}
            var Q14;
            {var subQ1=sQuery(id+"F0.wireOp",EDGE,"E1");var subQ3=sQuery(id+"F0.wireOp",EDGE,"E22.2.3");var subQ4=makeQuery(id+"F0.imprint","INTERSECT",VERTEX,{"derivedFrom":[subQ1,subQ3]});Q14=makeQuery(id+"F0.imprint","IMPRINT",FACE,{"disambiguationData":[TD([[makeQuery(id+"F0.imprint","IMPRINT",EDGE,{"disambiguationData":[TD([[subQ4,-1.0]])],"derivedFrom":subQ3}),-1.0]])]});}
            var Q15;
            {var subQ6=sQuery(id+"F0.wireOp",EDGE,"E0");var subQ11=sQuery(id+"F0.wireOp",EDGE,"E20.1.3");var subQ13=makeQuery(id+"F0.imprint","INTERSECT",VERTEX,{"derivedFrom":[subQ6,subQ11]});Q15=makeQuery(id+"F0.imprint","IMPRINT",FACE,{"disambiguationData":[TD([[makeQuery(id+"F0.imprint","IMPRINT",EDGE,{"disambiguationData":[TD([[subQ13,-1.0]])],"derivedFrom":subQ6}),1.0]])]});}
            var Q16;
            {var subQ0=sQuery(id+"F0.wireOp",EDGE,"E20.1.0");var subQ1=sQuery(id+"F0.wireOp",EDGE,"E0");var subQ2=makeQuery(id+"F0.imprint","INTERSECT",VERTEX,{"derivedFrom":[subQ1,subQ0]});Q16=makeQuery(id+"F0.imprint","IMPRINT",FACE,{"disambiguationData":[TD([[makeQuery(id+"F0.imprint","IMPRINT",EDGE,{"disambiguationData":[TD([[subQ2,-1.0]])],"derivedFrom":subQ1}),1.0]])]});}
            var Q17;
            {var subQ0=sQuery(id+"F0.wireOp",EDGE,"E21.3.0");var subQ1=sQuery(id+"F0.wireOp",EDGE,"E0");var subQ2=makeQuery(id+"F0.imprint","INTERSECT",VERTEX,{"derivedFrom":[subQ1,subQ0]});Q17=makeQuery(id+"F0.imprint","IMPRINT",FACE,{"disambiguationData":[TD([[makeQuery(id+"F0.imprint","IMPRINT",EDGE,{"disambiguationData":[TD([[subQ2,-1.0]])],"derivedFrom":subQ1}),1.0]])]});}
            var Q18;
            {var subQ0=sQuery(id+"F0.wireOp",EDGE,"E22.3.0");var subQ1=sQuery(id+"F0.wireOp",EDGE,"E0");var subQ2=makeQuery(id+"F0.imprint","INTERSECT",VERTEX,{"derivedFrom":[subQ1,subQ0]});Q18=makeQuery(id+"F0.imprint","IMPRINT",FACE,{"disambiguationData":[TD([[makeQuery(id+"F0.imprint","IMPRINT",EDGE,{"disambiguationData":[TD([[subQ2,-1.0]])],"derivedFrom":subQ1}),1.0]])]});}
            var Q19;
            {var subQ0=sQuery(id+"F0.wireOp",EDGE,"E20.2.0");var subQ1=sQuery(id+"F0.wireOp",EDGE,"E0");var subQ2=makeQuery(id+"F0.imprint","INTERSECT",VERTEX,{"derivedFrom":[subQ1,subQ0]});Q19=makeQuery(id+"F0.imprint","IMPRINT",FACE,{"disambiguationData":[TD([[makeQuery(id+"F0.imprint","IMPRINT",EDGE,{"disambiguationData":[TD([[subQ2,-1.0]])],"derivedFrom":subQ1}),1.0]])]});}
            var Q20;
            {var subQ6=sQuery(id+"F0.wireOp",EDGE,"E0");var subQ11=sQuery(id+"F0.wireOp",EDGE,"E20.2.3");var subQ12=makeQuery(id+"F0.imprint","INTERSECT",VERTEX,{"derivedFrom":[subQ6,subQ11]});Q20=makeQuery(id+"F0.imprint","IMPRINT",FACE,{"disambiguationData":[TD([[makeQuery(id+"F0.imprint","IMPRINT",EDGE,{"disambiguationData":[TD([[subQ12,-1.0]])],"derivedFrom":subQ6}),1.0]])]});}
            var Q21;
            {var subQ1=sQuery(id+"F0.wireOp",EDGE,"E1");var subQ3=sQuery(id+"F0.wireOp",EDGE,"E22.3.3");var subQ4=makeQuery(id+"F0.imprint","INTERSECT",VERTEX,{"derivedFrom":[subQ1,subQ3]});Q21=makeQuery(id+"F0.imprint","IMPRINT",FACE,{"disambiguationData":[TD([[makeQuery(id+"F0.imprint","IMPRINT",EDGE,{"disambiguationData":[TD([[subQ4,-1.0]])],"derivedFrom":subQ3}),-1.0]])]});}
            var Q22;
            {var subQ1=sQuery(id+"F0.wireOp",EDGE,"E1");var subQ3=sQuery(id+"F0.wireOp",EDGE,"E21.2.0");var subQ4=makeQuery(id+"F0.imprint","INTERSECT",VERTEX,{"derivedFrom":[subQ1,subQ3]});Q22=makeQuery(id+"F0.imprint","IMPRINT",FACE,{"disambiguationData":[TD([[makeQuery(id+"F0.imprint","IMPRINT",EDGE,{"disambiguationData":[TD([[subQ4,-1.0]])],"derivedFrom":subQ3}),1.0]])]});}
            var Q23;
            {var subQ0=sQuery(id+"F0.wireOp",EDGE,"E21.2.0");var subQ1=sQuery(id+"F0.wireOp",EDGE,"E0");var subQ2=makeQuery(id+"F0.imprint","INTERSECT",VERTEX,{"derivedFrom":[subQ1,subQ0]});Q23=makeQuery(id+"F0.imprint","IMPRINT",FACE,{"disambiguationData":[TD([[makeQuery(id+"F0.imprint","IMPRINT",EDGE,{"disambiguationData":[TD([[subQ2,-1.0]])],"derivedFrom":subQ1}),1.0]])]});}
            var Q24;
            {var subQ0=sQuery(id+"F0.wireOp",EDGE,"E22.2.0");var subQ1=sQuery(id+"F0.wireOp",EDGE,"E0");var subQ2=makeQuery(id+"F0.imprint","INTERSECT",VERTEX,{"derivedFrom":[subQ1,subQ0]});Q24=makeQuery(id+"F0.imprint","IMPRINT",FACE,{"disambiguationData":[TD([[makeQuery(id+"F0.imprint","IMPRINT",EDGE,{"disambiguationData":[TD([[subQ2,-1.0]])],"derivedFrom":subQ1}),1.0]])]});}
            extrude(context, id + "F2", {"entities" : qUnion([Q0, Q1, Q2, Q3, Q4, Q5, Q6, Q7, Q8, Q9, Q10, Q11, Q12, Q13, Q14, Q15, Q16, Q17, Q18, Q19, Q20, Q21, Q22, Q23, Q24]), "operationType" : NewBodyOperationType.ADD, "oppositeDirection" : true, "depth" : 8 * mm});
        }
        {
            var Q0;
            {var subQ5=sQuery(id+"F0.wireOp",EDGE,"E13.MirrorCS");var subQ6=sQuery(id+"F0.wireOp",EDGE,"E0");var subQ7=makeQuery(id+"F0.imprint","INTERSECT",VERTEX,{"derivedFrom":[subQ6,subQ5]});Q0=makeQuery(id+"F0.imprint","IMPRINT",FACE,{"disambiguationData":[TD([[makeQuery(id+"F0.imprint","IMPRINT",EDGE,{"disambiguationData":[TD([[subQ7,-1.0]])],"derivedFrom":subQ6}),1.0]])]});}
            var Q1;
            {var subQ0=sQuery(id+"F0.wireOp",EDGE,"E5.MirrorCS");var subQ1=sQuery(id+"F0.wireOp",EDGE,"E2");var subQ2=makeQuery(id+"F0.imprint","INTERSECT",VERTEX,{"derivedFrom":[subQ1,subQ0]});Q1=makeQuery(id+"F0.imprint","IMPRINT",FACE,{"disambiguationData":[TD([[makeQuery(id+"F0.imprint","IMPRINT",EDGE,{"disambiguationData":[TD([[subQ2,1.0]])],"derivedFrom":subQ1}),1.0]])]});}
            var Q2;
            {var subQ1=sQuery(id+"F0.wireOp",EDGE,"E10");Q2=makeQuery(id+"F0.imprint","IMPRINT",FACE,{"disambiguationData":[TD([[makeQuery(id+"F0.imprint","IMPRINT",EDGE,{"derivedFrom":subQ1}),-1.0]])]});}
            var Q3;
            {var subQ0=sQuery(id+"F0.wireOp",EDGE,"E20.1.3");var subQ1=sQuery(id+"F0.wireOp",EDGE,"E20.1.2");var subQ2=makeQuery(id+"F0.imprint","INTERSECT",VERTEX,{"derivedFrom":[subQ1,subQ0]});Q3=makeQuery(id+"F0.imprint","IMPRINT",FACE,{"disambiguationData":[TD([[makeQuery(id+"F0.imprint","IMPRINT",EDGE,{"disambiguationData":[TD([[subQ2,1.0]])],"derivedFrom":subQ1}),1.0]])]});}
            var Q4;
            {var subQ0=sQuery(id+"F0.wireOp",EDGE,"E21.1.1");Q4=makeQuery(id+"F0.imprint","IMPRINT",FACE,{"disambiguationData":[TD([[makeQuery(id+"F0.imprint","IMPRINT",EDGE,{"derivedFrom":subQ0}),-1.0]])]});}
            var Q5;
            {var subQ6=sQuery(id+"F0.wireOp",EDGE,"E0");var subQ12=sQuery(id+"F0.wireOp",EDGE,"E21.1.3");var subQ13=makeQuery(id+"F0.imprint","INTERSECT",VERTEX,{"derivedFrom":[subQ6,subQ12]});Q5=makeQuery(id+"F0.imprint","IMPRINT",FACE,{"disambiguationData":[TD([[makeQuery(id+"F0.imprint","IMPRINT",EDGE,{"disambiguationData":[TD([[subQ13,-1.0]])],"derivedFrom":subQ6}),1.0]])]});}
            var Q6;
            {var subQ0=sQuery(id+"F0.wireOp",EDGE,"E20.2.3");var subQ1=sQuery(id+"F0.wireOp",EDGE,"E20.2.2");var subQ2=makeQuery(id+"F0.imprint","INTERSECT",VERTEX,{"derivedFrom":[subQ1,subQ0]});Q6=makeQuery(id+"F0.imprint","IMPRINT",FACE,{"disambiguationData":[TD([[makeQuery(id+"F0.imprint","IMPRINT",EDGE,{"disambiguationData":[TD([[subQ2,1.0]])],"derivedFrom":subQ1}),1.0]])]});}
            var Q7;
            {var subQ0=sQuery(id+"F0.wireOp",EDGE,"E21.2.1");Q7=makeQuery(id+"F0.imprint","IMPRINT",FACE,{"disambiguationData":[TD([[makeQuery(id+"F0.imprint","IMPRINT",EDGE,{"derivedFrom":subQ0}),-1.0]])]});}
            var Q8;
            {var subQ9=sQuery(id+"F0.wireOp",EDGE,"E21.2.3");var subQ10=sQuery(id+"F0.wireOp",EDGE,"E0");var subQ11=makeQuery(id+"F0.imprint","INTERSECT",VERTEX,{"derivedFrom":[subQ10,subQ9]});Q8=makeQuery(id+"F0.imprint","IMPRINT",FACE,{"disambiguationData":[TD([[makeQuery(id+"F0.imprint","IMPRINT",EDGE,{"disambiguationData":[TD([[subQ11,-1.0]])],"derivedFrom":subQ10}),1.0]])]});}
            var Q9;
            {var subQ10=sQuery(id+"F0.wireOp",EDGE,"E0");var subQ12=sQuery(id+"F0.wireOp",EDGE,"E21.3.3");var subQ13=makeQuery(id+"F0.imprint","INTERSECT",VERTEX,{"derivedFrom":[subQ10,subQ12]});Q9=makeQuery(id+"F0.imprint","IMPRINT",FACE,{"disambiguationData":[TD([[makeQuery(id+"F0.imprint","IMPRINT",EDGE,{"disambiguationData":[TD([[subQ13,-1.0]])],"derivedFrom":subQ10}),1.0]])]});}
            var Q10;
            {var subQ0=sQuery(id+"F0.wireOp",EDGE,"E21.3.1");Q10=makeQuery(id+"F0.imprint","IMPRINT",FACE,{"disambiguationData":[TD([[makeQuery(id+"F0.imprint","IMPRINT",EDGE,{"derivedFrom":subQ0}),-1.0]])]});}
            var Q11;
            {var subQ0=sQuery(id+"F0.wireOp",EDGE,"E20.3.3");var subQ1=sQuery(id+"F0.wireOp",EDGE,"E20.3.2");var subQ2=makeQuery(id+"F0.imprint","INTERSECT",VERTEX,{"derivedFrom":[subQ1,subQ0]});Q11=makeQuery(id+"F0.imprint","IMPRINT",FACE,{"disambiguationData":[TD([[makeQuery(id+"F0.imprint","IMPRINT",EDGE,{"disambiguationData":[TD([[subQ2,1.0]])],"derivedFrom":subQ1}),1.0]])]});}
            extrude(context, id + "F3", {"entities" : qUnion([Q0, Q1, Q2, Q3, Q4, Q5, Q6, Q7, Q8, Q9, Q10, Q11]), "operationType" : NewBodyOperationType.ADD, "oppositeDirection" : true, "depth" : 4 * mm});
        }
        {
            var Q0;
            {var subQ7=sQuery(id+"F0.wireOp",EDGE,"E5.MirrorCS");var subQ11=sQuery(id+"F0.wireOp",EDGE,"E0");var subQ13=makeQuery(id+"F0.imprint","INTERSECT",VERTEX,{"derivedFrom":[subQ11,subQ7]});Q0=makeQuery(id+"F0.imprint","IMPRINT",FACE,{"disambiguationData":[TD([[makeQuery(id+"F0.imprint","IMPRINT",EDGE,{"disambiguationData":[TD([[subQ13,-1.0]])],"derivedFrom":subQ11}),1.0]])]});}
            var Q1;
            {var subQ0=sQuery(id+"F0.wireOp",EDGE,"E4");var subQ1=sQuery(id+"F0.wireOp",EDGE,"E3.MirrorCS");var subQ2=makeQuery(id+"F0.imprint","INTERSECT",VERTEX,{"derivedFrom":[subQ1,subQ0]});Q1=makeQuery(id+"F0.imprint","IMPRINT",FACE,{"disambiguationData":[TD([[makeQuery(id+"F0.imprint","IMPRINT",EDGE,{"disambiguationData":[TD([[subQ2,1.0]])],"derivedFrom":subQ1}),-1.0]])]});}
            var Q2;
            {var subQ0=sQuery(id+"F0.wireOp",EDGE,"E5.MirrorCS");var subQ1=sQuery(id+"F0.wireOp",EDGE,"E2");var subQ2=makeQuery(id+"F0.imprint","INTERSECT",VERTEX,{"derivedFrom":[subQ1,subQ0]});Q2=makeQuery(id+"F0.imprint","IMPRINT",FACE,{"disambiguationData":[TD([[makeQuery(id+"F0.imprint","IMPRINT",EDGE,{"disambiguationData":[TD([[subQ2,1.0]])],"derivedFrom":subQ1}),1.0]])]});}
            var Q3;
            {var subQ0=sQuery(id+"F0.wireOp",EDGE,"E20.3.1");var subQ1=sQuery(id+"F0.wireOp",EDGE,"E19.MirrorCS");var subQ2=makeQuery(id+"F0.imprint","INTERSECT",VERTEX,{"derivedFrom":[subQ1,subQ0]});Q3=makeQuery(id+"F0.imprint","IMPRINT",FACE,{"disambiguationData":[TD([[makeQuery(id+"F0.imprint","IMPRINT",EDGE,{"disambiguationData":[TD([[subQ2,-1.0]])],"derivedFrom":subQ1}),1.0]])]});}
            var Q4;
            {var subQ0=sQuery(id+"F0.wireOp",EDGE,"E20.3.0");var subQ1=sQuery(id+"F0.wireOp",EDGE,"E0");var subQ2=makeQuery(id+"F0.imprint","INTERSECT",VERTEX,{"derivedFrom":[subQ1,subQ0]});Q4=makeQuery(id+"F0.imprint","IMPRINT",FACE,{"disambiguationData":[TD([[makeQuery(id+"F0.imprint","IMPRINT",EDGE,{"disambiguationData":[TD([[subQ2,1.0]])],"derivedFrom":subQ1}),1.0]])]});}
            var Q5;
            {var subQ0=sQuery(id+"F0.wireOp",EDGE,"E20.3.3");var subQ1=sQuery(id+"F0.wireOp",EDGE,"E20.3.2");var subQ2=makeQuery(id+"F0.imprint","INTERSECT",VERTEX,{"derivedFrom":[subQ1,subQ0]});Q5=makeQuery(id+"F0.imprint","IMPRINT",FACE,{"disambiguationData":[TD([[makeQuery(id+"F0.imprint","IMPRINT",EDGE,{"disambiguationData":[TD([[subQ2,1.0]])],"derivedFrom":subQ1}),1.0]])]});}
            var Q6;
            {var subQ0=sQuery(id+"F0.wireOp",EDGE,"E20.2.1");var subQ1=sQuery(id+"F0.wireOp",EDGE,"E20.2.0");var subQ2=makeQuery(id+"F0.imprint","INTERSECT",VERTEX,{"derivedFrom":[subQ1,subQ0]});Q6=makeQuery(id+"F0.imprint","IMPRINT",FACE,{"disambiguationData":[TD([[makeQuery(id+"F0.imprint","IMPRINT",EDGE,{"disambiguationData":[TD([[subQ2,-1.0]])],"derivedFrom":subQ1}),-1.0]])]});}
            var Q7;
            {var subQ0=sQuery(id+"F0.wireOp",EDGE,"E20.2.3");var subQ1=sQuery(id+"F0.wireOp",EDGE,"E20.2.2");var subQ2=makeQuery(id+"F0.imprint","INTERSECT",VERTEX,{"derivedFrom":[subQ1,subQ0]});Q7=makeQuery(id+"F0.imprint","IMPRINT",FACE,{"disambiguationData":[TD([[makeQuery(id+"F0.imprint","IMPRINT",EDGE,{"disambiguationData":[TD([[subQ2,1.0]])],"derivedFrom":subQ1}),1.0]])]});}
            var Q8;
            {var subQ6=sQuery(id+"F0.wireOp",EDGE,"E0");var subQ11=sQuery(id+"F0.wireOp",EDGE,"E20.2.3");var subQ12=makeQuery(id+"F0.imprint","INTERSECT",VERTEX,{"derivedFrom":[subQ6,subQ11]});Q8=makeQuery(id+"F0.imprint","IMPRINT",FACE,{"disambiguationData":[TD([[makeQuery(id+"F0.imprint","IMPRINT",EDGE,{"disambiguationData":[TD([[subQ12,-1.0]])],"derivedFrom":subQ6}),1.0]])]});}
            var Q9;
            {var subQ0=sQuery(id+"F0.wireOp",EDGE,"E20.1.1");var subQ1=sQuery(id+"F0.wireOp",EDGE,"E20.1.0");var subQ2=makeQuery(id+"F0.imprint","INTERSECT",VERTEX,{"derivedFrom":[subQ1,subQ0]});Q9=makeQuery(id+"F0.imprint","IMPRINT",FACE,{"disambiguationData":[TD([[makeQuery(id+"F0.imprint","IMPRINT",EDGE,{"disambiguationData":[TD([[subQ2,-1.0]])],"derivedFrom":subQ1}),-1.0]])]});}
            var Q10;
            {var subQ6=sQuery(id+"F0.wireOp",EDGE,"E0");var subQ11=sQuery(id+"F0.wireOp",EDGE,"E20.1.3");var subQ13=makeQuery(id+"F0.imprint","INTERSECT",VERTEX,{"derivedFrom":[subQ6,subQ11]});Q10=makeQuery(id+"F0.imprint","IMPRINT",FACE,{"disambiguationData":[TD([[makeQuery(id+"F0.imprint","IMPRINT",EDGE,{"disambiguationData":[TD([[subQ13,-1.0]])],"derivedFrom":subQ6}),1.0]])]});}
            var Q11;
            {var subQ0=sQuery(id+"F0.wireOp",EDGE,"E20.1.3");var subQ1=sQuery(id+"F0.wireOp",EDGE,"E20.1.2");var subQ2=makeQuery(id+"F0.imprint","INTERSECT",VERTEX,{"derivedFrom":[subQ1,subQ0]});Q11=makeQuery(id+"F0.imprint","IMPRINT",FACE,{"disambiguationData":[TD([[makeQuery(id+"F0.imprint","IMPRINT",EDGE,{"disambiguationData":[TD([[subQ2,1.0]])],"derivedFrom":subQ1}),1.0]])]});}
            extrude(context, id + "F4", {"entities" : qUnion([Q0, Q1, Q2, Q3, Q4, Q5, Q6, Q7, Q8, Q9, Q10, Q11]), "operationType" : NewBodyOperationType.REMOVE, "depth" : 4 * mm, "hasSecondDirection" : true, "secondDirectionOppositeDirection" : true, "secondDirectionDepth" : 10 * mm});
        }
        {
            var Q0;
            Q0=makeQuery(id+"F1.opExtrude","CAP_FACE",FACE,{"disambiguationData":[OSD([sQuery(id+"F0.wireOp",EDGE,"E0"),sQuery(id+"F0.wireOp",EDGE,"E23")])],"isStart":false});
            var sketch = newSketch(context, id + "F5", { "sketchPlane" : qUnion([Q0])});
            skLineSegment(sketch, "E24.bottom", {"start": v(29, -29) * mm, "end": v(-29, -29) * mm});
            skLineSegment(sketch, "E24.top", {"start": v(29, 29) * mm, "end": v(-29, 29) * mm});
            skLineSegment(sketch, "E24.left", {"start": v(29, -29) * mm, "end": v(29, 29) * mm});
            skLineSegment(sketch, "E24.right", {"start": v(-29, -29) * mm, "end": v(-29, 29) * mm});
            skPoint(sketch, "E24.middle", {"position": v(0, 0) * mm});
            skLineSegment(sketch, "E25", {"start": v(-18, 29) * mm, "end": v(0, 44) * mm});
            skLineSegment(sketch, "E26.MirrorCS", {"start": v(18, 29) * mm, "end": v(0, 44) * mm});
            skSolve(sketch);
        }
        {
            var Q0;
            Q0=makeQuery(id+"F5.imprint","IMPRINT",FACE,{"disambiguationData":[TD([[makeQuery(id+"F5.imprint","IMPRINT",EDGE,{"derivedFrom":sQuery(id+"F5.wireOp",EDGE,"E24.bottom")}),-1.0]])]});
            var Q1;
            {var subQ0=sQuery(id+"F5.wireOp",EDGE,"E25");Q1=makeQuery(id+"F5.imprint","IMPRINT",FACE,{"disambiguationData":[TD([[makeQuery(id+"F5.imprint","IMPRINT",EDGE,{"derivedFrom":subQ0}),-1.0]])]});}
            extrude(context, id + "F6", {"entities" : qUnion([Q0, Q1]), "operationType" : NewBodyOperationType.REMOVE, "oppositeDirection" : true, "offsetDistance" : 25 * mm, "depth" : 6 * mm});
        }
        {
            var Q0;
            Q0=makeQuery(id+"F6.boolean.opBoolean","COPY",EDGE,{"derivedFrom":makeQuery(id+"F6.opExtrude","SWEPT_EDGE",EDGE,{"disambiguationData":[OSD([sQuery(id+"F5.wireOp",EDGE,"E25"),sQuery(id+"F5.wireOp",EDGE,"E26.MirrorCS")])]})});
            var Q1;
            Q1=makeQuery(id+"F6.boolean.opBoolean","COPY",EDGE,{"derivedFrom":makeQuery(id+"F6.opExtrude","SWEPT_EDGE",EDGE,{"disambiguationData":[OSD([sQuery(id+"F5.wireOp",EDGE,"E24.top"),sQuery(id+"F5.wireOp",EDGE,"E25")])]})});
            var Q2;
            Q2=makeQuery(id+"F6.boolean.opBoolean","COPY",EDGE,{"derivedFrom":makeQuery(id+"F6.opExtrude","SWEPT_EDGE",EDGE,{"disambiguationData":[OSD([sQuery(id+"F5.wireOp",EDGE,"E24.top"),sQuery(id+"F5.wireOp",EDGE,"E26.MirrorCS")])]})});
            fillet(context, id + "F7", {"entities" : qUnion([Q0, Q1, Q2]), "radius" : 5 * mm, "tangentPropagation" : true, "allowEdgeOverflow" : false});
        }
        {
            var Q0;
            {var subQ0=sQuery(id+"F0.wireOp",EDGE,"E22.3.1");var subQ1=sQuery(id+"F0.wireOp",EDGE,"E22.1.2");var subQ2=sQuery(id+"F0.wireOp",EDGE,"E22.1.1");var subQ3=sQuery(id+"F0.wireOp",EDGE,"E21.3.0");var subQ4=sQuery(id+"F0.wireOp",EDGE,"E16");var subQ5=sQuery(id+"F0.wireOp",EDGE,"E11.MirrorCS");var subQ6=sQuery(id+"F0.wireOp",EDGE,"E10");var subQ7=sQuery(id+"F0.wireOp",EDGE,"E22.2.3");var subQ8=sQuery(id+"F0.wireOp",EDGE,"E22.2.2");var subQ9=sQuery(id+"F0.wireOp",EDGE,"E22.2.1");var subQ10=sQuery(id+"F0.wireOp",EDGE,"E22.1.3");var subQ11=sQuery(id+"F0.wireOp",EDGE,"E21.3.2");var subQ12=sQuery(id+"F0.wireOp",EDGE,"E21.3.1");var subQ13=sQuery(id+"F0.wireOp",EDGE,"E18.MirrorCS");var subQ14=sQuery(id+"F0.wireOp",EDGE,"E22.3.2");var subQ15=sQuery(id+"F0.wireOp",EDGE,"E23");var subQ16=sQuery(id+"F0.wireOp",EDGE,"E21.1.2");var subQ17=sQuery(id+"F0.wireOp",EDGE,"E21.1.1");var subQ18=sQuery(id+"F0.wireOp",EDGE,"E12");var subQ19=sQuery(id+"F0.wireOp",EDGE,"E22.3.3");var subQ20=sQuery(id+"F0.wireOp",EDGE,"E19.MirrorCS");var subQ21=sQuery(id+"F0.wireOp",EDGE,"E21.1.0");var subQ22=sQuery(id+"F0.wireOp",EDGE,"E21.2.0");var subQ23=sQuery(id+"F0.wireOp",EDGE,"E21.2.2");var subQ24=sQuery(id+"F0.wireOp",EDGE,"E21.2.1");Q0=makeQuery(id+"F4.boolean.opBoolean","SPLIT",FACE,{"disambiguationData":[TD([makeQuery(id+"F1.opExtrude","SWEPT_FACE",FACE,{"disambiguationData":[OSD([subQ15])]})])],"derivedFrom":makeQuery(id+"F2.opExtrude","CAP_FACE",FACE,{"disambiguationData":[OSD([sQuery(id+"F0.wireOp",EDGE,"E0"),subQ6,subQ5,subQ18,subQ4,subQ13,subQ20,subQ21,subQ17,subQ16,subQ22,subQ24,subQ23,subQ3,subQ12,subQ11,subQ2,subQ1,subQ10,subQ9,subQ8,subQ7,subQ0,subQ14,subQ19,subQ15])],"isStart":false})});}
            var sketch = newSketch(context, id + "F8", { "sketchPlane" : qUnion([Q0])});
            skCircle(sketch, "E27", {"center": v(0, 42) * mm, "radius": 2 * mm});
            skCircle(sketch, "E28.1.0", {"center": v(-42, 0) * mm, "radius": 2 * mm});
            skCircle(sketch, "E28.2.0", {"center": v(0, -42) * mm, "radius": 2 * mm});
            skCircle(sketch, "E28.3.0", {"center": v(42, 0) * mm, "radius": 2 * mm});
            skPoint(sketch, "E28.center", {"position": v(0, 0) * mm});
            skSolve(sketch);
        }
        {
            var Q0;
            Q0 = qSketchRegion(id + "F8", true);
            extrude(context, id + "F9", {"entities" : qUnion([Q0]), "operationType" : NewBodyOperationType.REMOVE, "oppositeDirection" : true, "depth" : 5 * mm});
        }
        {
            var Q0;
            Q0=makeQuery(id+"F4.boolean.opBoolean","COPY",FACE,{"derivedFrom":makeQuery(id+"F4.opExtrude","SWEPT_FACE",FACE,{"disambiguationData":[OSD([sQuery(id+"F0.wireOp",EDGE,"E2"),sQuery(id+"F0.wireOp",EDGE,"E3.MirrorCS")])]})});
            var sketch = newSketch(context, id + "F10", { "sketchPlane" : qUnion([Q0])});
            skArc(sketch, "E29", {"start": v(-15.5, 0) * mm, "mid": v(-17.5, -2) * mm, "end": v(-15.5, -4) * mm});
            skArc(sketch, "E30.MirrorCS", {"start": v(15.5, 0) * mm, "mid": v(17.5, -2) * mm, "end": v(15.5, -4) * mm});
            skLineSegment(sketch, "E31", {"start": v(-15.5, 0) * mm, "end": v(15.5, 0) * mm});
            skLineSegment(sketch, "E32", {"start": v(-15.5, -4) * mm, "end": v(15.5, -4) * mm});
            skSolve(sketch);
        }
        {
            var Q0;
            {var subQ2=sQuery(id+"F10.wireOp",EDGE,"E32");Q0=makeQuery(id+"F10.imprint","IMPRINT",FACE,{"disambiguationData":[TD([[makeQuery(id+"F10.imprint","IMPRINT",EDGE,{"derivedFrom":subQ2}),1.0]])]});}
            var Q1;
            {var subQ0=sQuery(id+"F10.wireOp",EDGE,"E30.MirrorCS");Q1=makeQuery(id+"F10.imprint","IMPRINT",FACE,{"disambiguationData":[TD([[makeQuery(id+"F10.imprint","IMPRINT",EDGE,{"derivedFrom":subQ0}),-1.0]])]});}
            var Q2;
            Q2=makeQuery(id+"F10.imprint","IMPRINT",FACE,{"disambiguationData":[TD([[makeQuery(id+"F10.imprint","IMPRINT",EDGE,{"derivedFrom":sQuery(id+"F10.wireOp",EDGE,"E29")}),1.0]])]});
            extrude(context, id + "F11", {"entities" : qUnion([Q0, Q1, Q2]), "operationType" : NewBodyOperationType.REMOVE, "depth" : 25 * mm, "offsetDistance" : 25 * mm});
        }
        {
            var Q0;
            {var subQ0=sQuery(id+"F0.wireOp",EDGE,"E22.1.1");Q0=makeQuery(id+"F3.boolean.opBoolean","MERGE",FACE,{"derivedFrom":[makeQuery(id+"F2.opExtrude","SWEPT_FACE",FACE,{"disambiguationData":[OSD([subQ0,sQuery(id+"F0.wireOp",EDGE,"E22.1.2")])]}),makeQuery(id+"F3.opExtrude","SWEPT_FACE",FACE,{"disambiguationData":[OSD([subQ0])]})]});}
            var sketch = newSketch(context, id + "F12", { "sketchPlane" : qUnion([Q0])});
            skArc(sketch, "E33", {"start": v(-15, 4) * mm, "mid": v(-17, 2) * mm, "end": v(-15, 0) * mm});
            skLineSegment(sketch, "E34", {"start": v(0, 0) * mm, "end": v(0, 10.52) * mm, "construction": true});
            skLineSegment(sketch, "E35", {"start": v(-15, 4) * mm, "end": v(16, 4) * mm});
            skLineSegment(sketch, "E36", {"start": v(-15, 0) * mm, "end": v(16, 0) * mm});
            skArc(sketch, "E37", {"start": v(16, 0) * mm, "mid": v(18, 2) * mm, "end": v(16, 4) * mm});
            skSolve(sketch);
        }
        {
            var Q0;
            {var subQ0=sQuery(id+"F12.wireOp",EDGE,"E36");Q0=makeQuery(id+"F12.imprint","IMPRINT",FACE,{"disambiguationData":[TD([[makeQuery(id+"F12.imprint","IMPRINT",EDGE,{"derivedFrom":subQ0}),1.0]])]});}
            var Q1;
            Q1=makeQuery(id+"F12.imprint","IMPRINT",FACE,{"disambiguationData":[TD([[makeQuery(id+"F12.imprint","IMPRINT",EDGE,{"derivedFrom":sQuery(id+"F12.wireOp",EDGE,"E33")}),1.0]])]});
            var Q2;
            {var subQ0=sQuery(id+"F12.wireOp",EDGE,"E37");Q2=makeQuery(id+"F12.imprint","IMPRINT",FACE,{"disambiguationData":[TD([[makeQuery(id+"F12.imprint","IMPRINT",EDGE,{"derivedFrom":subQ0}),1.0]])]});}
            extrude(context, id + "F13", {"entities" : qUnion([Q0, Q1, Q2]), "operationType" : NewBodyOperationType.REMOVE, "depth" : 45 * mm, "offsetDistance" : 25 * mm});
        }
        {
            var Q0;
            Q0=makeQuery(id+"F2.opExtrude","SWEPT_FACE",FACE,{"disambiguationData":[OSD([sQuery(id+"F0.wireOp",EDGE,"E21.1.1"),sQuery(id+"F0.wireOp",EDGE,"E21.1.2")])]});
            var sketch = newSketch(context, id + "F14", { "sketchPlane" : qUnion([Q0])});
            skArc(sketch, "E38", {"start": v(-8, -16) * mm, "mid": v(-6, -18) * mm, "end": v(-4, -16) * mm});
            skLineSegment(sketch, "E39", {"start": v(-8, -16) * mm, "end": v(-8, 15) * mm});
            skLineSegment(sketch, "E40", {"start": v(-8, 15) * mm, "end": v(-4, 15) * mm});
            skLineSegment(sketch, "E41", {"start": v(-4, 15) * mm, "end": v(-4, -16) * mm});
            skArc(sketch, "E42", {"start": v(-4, 15) * mm, "mid": v(-6, 17) * mm, "end": v(-8, 15) * mm});
            skSolve(sketch);
        }
        {
            var Q0;
            Q0=makeQuery(id+"F14.imprint","IMPRINT",FACE,{"disambiguationData":[TD([[makeQuery(id+"F14.imprint","IMPRINT",EDGE,{"derivedFrom":sQuery(id+"F14.wireOp",EDGE,"E38")}),1.0]])]});
            var Q1;
            {var subQ2=makeQuery(id+"F2.opExtrude","SWEPT_EDGE",EDGE,{"disambiguationData":[OSD([sQuery(id+"F0.wireOp",EDGE,"E21.1.0"),sQuery(id+"F0.wireOp",EDGE,"E21.1.1")])]});Q1=makeQuery(id+"F14.imprint","IMPRINT",FACE,{"disambiguationData":[TD([[makeQuery(id+"F14.imprint","IMPRINT",EDGE,{"derivedFrom":subQ2}),1.0]])]});}
            var Q2;
            Q2=makeQuery(id+"F14.imprint","IMPRINT",FACE,{"disambiguationData":[TD([[makeQuery(id+"F14.imprint","IMPRINT",EDGE,{"derivedFrom":sQuery(id+"F14.wireOp",EDGE,"E40")}),1.0]])]});
            var Q3;
            {var subQ3=sQuery(id+"F14.wireOp",EDGE,"E40");Q3=makeQuery(id+"F14.imprint","IMPRINT",FACE,{"disambiguationData":[TD([[makeQuery(id+"F14.imprint","IMPRINT",EDGE,{"derivedFrom":subQ3}),-1.0]])]});}
            extrude(context, id + "F15", {"entities" : qUnion([Q0, Q1, Q2, Q3]), "operationType" : NewBodyOperationType.REMOVE, "depth" : 45 * mm, "offsetDistance" : 25 * mm});
        }
        {
            var Q0;
            Q0=makeQuery(id+"F1.opExtrude","CAP_EDGE",EDGE,{"disambiguationData":[OSD([sQuery(id+"F0.wireOp",EDGE,"E0")])],"isStart":false});
            chamfer(context, id + "F16", {"entities" : qUnion([Q0]), "chamferType" : ChamferType.TWO_OFFSETS, "width1" : 2 * mm, "oppositeDirection" : false, "width2" : 3 * mm, "tangentPropagation" : true});
        }
        {
            var Q0;
            {var subQ0=sQuery(id+"F0.wireOp",EDGE,"E22.3.1");var subQ1=sQuery(id+"F0.wireOp",EDGE,"E22.1.2");var subQ2=sQuery(id+"F0.wireOp",EDGE,"E22.1.1");var subQ3=sQuery(id+"F0.wireOp",EDGE,"E21.3.0");var subQ4=sQuery(id+"F0.wireOp",EDGE,"E16");var subQ5=sQuery(id+"F0.wireOp",EDGE,"E11.MirrorCS");var subQ6=sQuery(id+"F0.wireOp",EDGE,"E10");var subQ7=sQuery(id+"F0.wireOp",EDGE,"E22.2.3");var subQ8=sQuery(id+"F0.wireOp",EDGE,"E22.2.2");var subQ9=sQuery(id+"F0.wireOp",EDGE,"E22.2.1");var subQ10=sQuery(id+"F0.wireOp",EDGE,"E22.1.3");var subQ11=sQuery(id+"F0.wireOp",EDGE,"E21.3.2");var subQ12=sQuery(id+"F0.wireOp",EDGE,"E21.3.1");var subQ13=sQuery(id+"F0.wireOp",EDGE,"E18.MirrorCS");var subQ14=sQuery(id+"F0.wireOp",EDGE,"E22.3.2");var subQ15=sQuery(id+"F0.wireOp",EDGE,"E23");var subQ16=sQuery(id+"F0.wireOp",EDGE,"E21.1.2");var subQ17=sQuery(id+"F0.wireOp",EDGE,"E21.1.1");var subQ18=sQuery(id+"F0.wireOp",EDGE,"E12");var subQ19=sQuery(id+"F0.wireOp",EDGE,"E22.3.3");var subQ20=sQuery(id+"F0.wireOp",EDGE,"E19.MirrorCS");var subQ21=sQuery(id+"F0.wireOp",EDGE,"E21.1.0");var subQ22=sQuery(id+"F0.wireOp",EDGE,"E21.2.0");var subQ23=sQuery(id+"F0.wireOp",EDGE,"E21.2.2");var subQ24=sQuery(id+"F0.wireOp",EDGE,"E21.2.1");Q0=makeQuery(id+"F4.boolean.opBoolean","SPLIT",FACE,{"disambiguationData":[TD([makeQuery(id+"F1.opExtrude","SWEPT_FACE",FACE,{"disambiguationData":[OSD([subQ15])]})])],"derivedFrom":makeQuery(id+"F2.opExtrude","CAP_FACE",FACE,{"disambiguationData":[OSD([sQuery(id+"F0.wireOp",EDGE,"E0"),subQ6,subQ5,subQ18,subQ4,subQ13,subQ20,subQ21,subQ17,subQ16,subQ22,subQ24,subQ23,subQ3,subQ12,subQ11,subQ2,subQ1,subQ10,subQ9,subQ8,subQ7,subQ0,subQ14,subQ19,subQ15])],"isStart":false})});}
            var sketch = newSketch(context, id + "F17", { "sketchPlane" : qUnion([Q0])});
            skCircle(sketch, "E43", {"center": v(0, 0) * mm, "radius": 9 * mm});
            skSolve(sketch);
        }
        {
            var Q0;
            Q0 = qSketchRegion(id + "F17", true);
            extrude(context, id + "F18", {"entities" : qUnion([Q0]), "operationType" : NewBodyOperationType.REMOVE, "oppositeDirection" : true, "depth" : 4 * mm, "offsetDistance" : 25 * mm});
        }
        {
            var Q0;
            Q0=makeQuery(id+"F4.boolean.opBoolean","INTERSECT",EDGE,{"derivedFrom":[makeQuery(id+"F2.opExtrude","CAP_FACE",FACE,{"disambiguationData":[OSD([sQuery(id+"F0.wireOp",EDGE,"E0"),sQuery(id+"F0.wireOp",EDGE,"E10"),sQuery(id+"F0.wireOp",EDGE,"E11.MirrorCS"),sQuery(id+"F0.wireOp",EDGE,"E12"),sQuery(id+"F0.wireOp",EDGE,"E16"),sQuery(id+"F0.wireOp",EDGE,"E18.MirrorCS"),sQuery(id+"F0.wireOp",EDGE,"E19.MirrorCS"),sQuery(id+"F0.wireOp",EDGE,"E21.1.0"),sQuery(id+"F0.wireOp",EDGE,"E21.1.1"),sQuery(id+"F0.wireOp",EDGE,"E21.1.2"),sQuery(id+"F0.wireOp",EDGE,"E21.2.0"),sQuery(id+"F0.wireOp",EDGE,"E21.2.1"),sQuery(id+"F0.wireOp",EDGE,"E21.2.2"),sQuery(id+"F0.wireOp",EDGE,"E21.3.0"),sQuery(id+"F0.wireOp",EDGE,"E21.3.1"),sQuery(id+"F0.wireOp",EDGE,"E21.3.2"),sQuery(id+"F0.wireOp",EDGE,"E22.1.1"),sQuery(id+"F0.wireOp",EDGE,"E22.1.2"),sQuery(id+"F0.wireOp",EDGE,"E22.1.3"),sQuery(id+"F0.wireOp",EDGE,"E22.2.1"),sQuery(id+"F0.wireOp",EDGE,"E22.2.2"),sQuery(id+"F0.wireOp",EDGE,"E22.2.3"),sQuery(id+"F0.wireOp",EDGE,"E22.3.1"),sQuery(id+"F0.wireOp",EDGE,"E22.3.2"),sQuery(id+"F0.wireOp",EDGE,"E22.3.3"),sQuery(id+"F0.wireOp",EDGE,"E23")])],"isStart":false}),makeQuery(id+"F4.opExtrude","SWEPT_FACE",FACE,{"disambiguationData":[OSD([sQuery(id+"F0.wireOp",EDGE,"E2"),sQuery(id+"F0.wireOp",EDGE,"E3.MirrorCS")])]})]});
            var Q1;
            Q1=makeQuery(id+"F4.boolean.opBoolean","INTERSECT",EDGE,{"derivedFrom":[makeQuery(id+"F2.opExtrude","CAP_FACE",FACE,{"disambiguationData":[OSD([sQuery(id+"F0.wireOp",EDGE,"E0"),sQuery(id+"F0.wireOp",EDGE,"E10"),sQuery(id+"F0.wireOp",EDGE,"E11.MirrorCS"),sQuery(id+"F0.wireOp",EDGE,"E12"),sQuery(id+"F0.wireOp",EDGE,"E16"),sQuery(id+"F0.wireOp",EDGE,"E18.MirrorCS"),sQuery(id+"F0.wireOp",EDGE,"E19.MirrorCS"),sQuery(id+"F0.wireOp",EDGE,"E21.1.0"),sQuery(id+"F0.wireOp",EDGE,"E21.1.1"),sQuery(id+"F0.wireOp",EDGE,"E21.1.2"),sQuery(id+"F0.wireOp",EDGE,"E21.2.0"),sQuery(id+"F0.wireOp",EDGE,"E21.2.1"),sQuery(id+"F0.wireOp",EDGE,"E21.2.2"),sQuery(id+"F0.wireOp",EDGE,"E21.3.0"),sQuery(id+"F0.wireOp",EDGE,"E21.3.1"),sQuery(id+"F0.wireOp",EDGE,"E21.3.2"),sQuery(id+"F0.wireOp",EDGE,"E22.1.1"),sQuery(id+"F0.wireOp",EDGE,"E22.1.2"),sQuery(id+"F0.wireOp",EDGE,"E22.1.3"),sQuery(id+"F0.wireOp",EDGE,"E22.2.1"),sQuery(id+"F0.wireOp",EDGE,"E22.2.2"),sQuery(id+"F0.wireOp",EDGE,"E22.2.3"),sQuery(id+"F0.wireOp",EDGE,"E22.3.1"),sQuery(id+"F0.wireOp",EDGE,"E22.3.2"),sQuery(id+"F0.wireOp",EDGE,"E22.3.3"),sQuery(id+"F0.wireOp",EDGE,"E23")])],"isStart":false}),makeQuery(id+"F4.opExtrude","SWEPT_FACE",FACE,{"disambiguationData":[OSD([sQuery(id+"F0.wireOp",EDGE,"E20.3.1"),sQuery(id+"F0.wireOp",EDGE,"E20.3.2")])]})]});
            var Q2;
            Q2=makeQuery(id+"F4.boolean.opBoolean","INTERSECT",EDGE,{"derivedFrom":[makeQuery(id+"F2.opExtrude","CAP_FACE",FACE,{"disambiguationData":[OSD([sQuery(id+"F0.wireOp",EDGE,"E0"),sQuery(id+"F0.wireOp",EDGE,"E10"),sQuery(id+"F0.wireOp",EDGE,"E11.MirrorCS"),sQuery(id+"F0.wireOp",EDGE,"E12"),sQuery(id+"F0.wireOp",EDGE,"E16"),sQuery(id+"F0.wireOp",EDGE,"E18.MirrorCS"),sQuery(id+"F0.wireOp",EDGE,"E19.MirrorCS"),sQuery(id+"F0.wireOp",EDGE,"E21.1.0"),sQuery(id+"F0.wireOp",EDGE,"E21.1.1"),sQuery(id+"F0.wireOp",EDGE,"E21.1.2"),sQuery(id+"F0.wireOp",EDGE,"E21.2.0"),sQuery(id+"F0.wireOp",EDGE,"E21.2.1"),sQuery(id+"F0.wireOp",EDGE,"E21.2.2"),sQuery(id+"F0.wireOp",EDGE,"E21.3.0"),sQuery(id+"F0.wireOp",EDGE,"E21.3.1"),sQuery(id+"F0.wireOp",EDGE,"E21.3.2"),sQuery(id+"F0.wireOp",EDGE,"E22.1.1"),sQuery(id+"F0.wireOp",EDGE,"E22.1.2"),sQuery(id+"F0.wireOp",EDGE,"E22.1.3"),sQuery(id+"F0.wireOp",EDGE,"E22.2.1"),sQuery(id+"F0.wireOp",EDGE,"E22.2.2"),sQuery(id+"F0.wireOp",EDGE,"E22.2.3"),sQuery(id+"F0.wireOp",EDGE,"E22.3.1"),sQuery(id+"F0.wireOp",EDGE,"E22.3.2"),sQuery(id+"F0.wireOp",EDGE,"E22.3.3"),sQuery(id+"F0.wireOp",EDGE,"E23")])],"isStart":false}),makeQuery(id+"F4.opExtrude","SWEPT_FACE",FACE,{"disambiguationData":[OSD([sQuery(id+"F0.wireOp",EDGE,"E20.1.1"),sQuery(id+"F0.wireOp",EDGE,"E20.1.2")])]})]});
            var Q3;
            Q3=makeQuery(id+"F4.boolean.opBoolean","INTERSECT",EDGE,{"derivedFrom":[makeQuery(id+"F2.opExtrude","CAP_FACE",FACE,{"disambiguationData":[OSD([sQuery(id+"F0.wireOp",EDGE,"E0"),sQuery(id+"F0.wireOp",EDGE,"E10"),sQuery(id+"F0.wireOp",EDGE,"E11.MirrorCS"),sQuery(id+"F0.wireOp",EDGE,"E12"),sQuery(id+"F0.wireOp",EDGE,"E16"),sQuery(id+"F0.wireOp",EDGE,"E18.MirrorCS"),sQuery(id+"F0.wireOp",EDGE,"E19.MirrorCS"),sQuery(id+"F0.wireOp",EDGE,"E21.1.0"),sQuery(id+"F0.wireOp",EDGE,"E21.1.1"),sQuery(id+"F0.wireOp",EDGE,"E21.1.2"),sQuery(id+"F0.wireOp",EDGE,"E21.2.0"),sQuery(id+"F0.wireOp",EDGE,"E21.2.1"),sQuery(id+"F0.wireOp",EDGE,"E21.2.2"),sQuery(id+"F0.wireOp",EDGE,"E21.3.0"),sQuery(id+"F0.wireOp",EDGE,"E21.3.1"),sQuery(id+"F0.wireOp",EDGE,"E21.3.2"),sQuery(id+"F0.wireOp",EDGE,"E22.1.1"),sQuery(id+"F0.wireOp",EDGE,"E22.1.2"),sQuery(id+"F0.wireOp",EDGE,"E22.1.3"),sQuery(id+"F0.wireOp",EDGE,"E22.2.1"),sQuery(id+"F0.wireOp",EDGE,"E22.2.2"),sQuery(id+"F0.wireOp",EDGE,"E22.2.3"),sQuery(id+"F0.wireOp",EDGE,"E22.3.1"),sQuery(id+"F0.wireOp",EDGE,"E22.3.2"),sQuery(id+"F0.wireOp",EDGE,"E22.3.3"),sQuery(id+"F0.wireOp",EDGE,"E23")])],"isStart":false}),makeQuery(id+"F4.opExtrude","SWEPT_FACE",FACE,{"disambiguationData":[OSD([sQuery(id+"F0.wireOp",EDGE,"E20.2.1"),sQuery(id+"F0.wireOp",EDGE,"E20.2.2")])]})]});
            chamfer(context, id + "F19", {"entities" : qUnion([Q0, Q1, Q2, Q3]), "chamferType" : ChamferType.TWO_OFFSETS, "width1" : 1 * mm, "oppositeDirection" : true, "width2" : 10 * mm, "tangentPropagation" : true});
        }
    });
